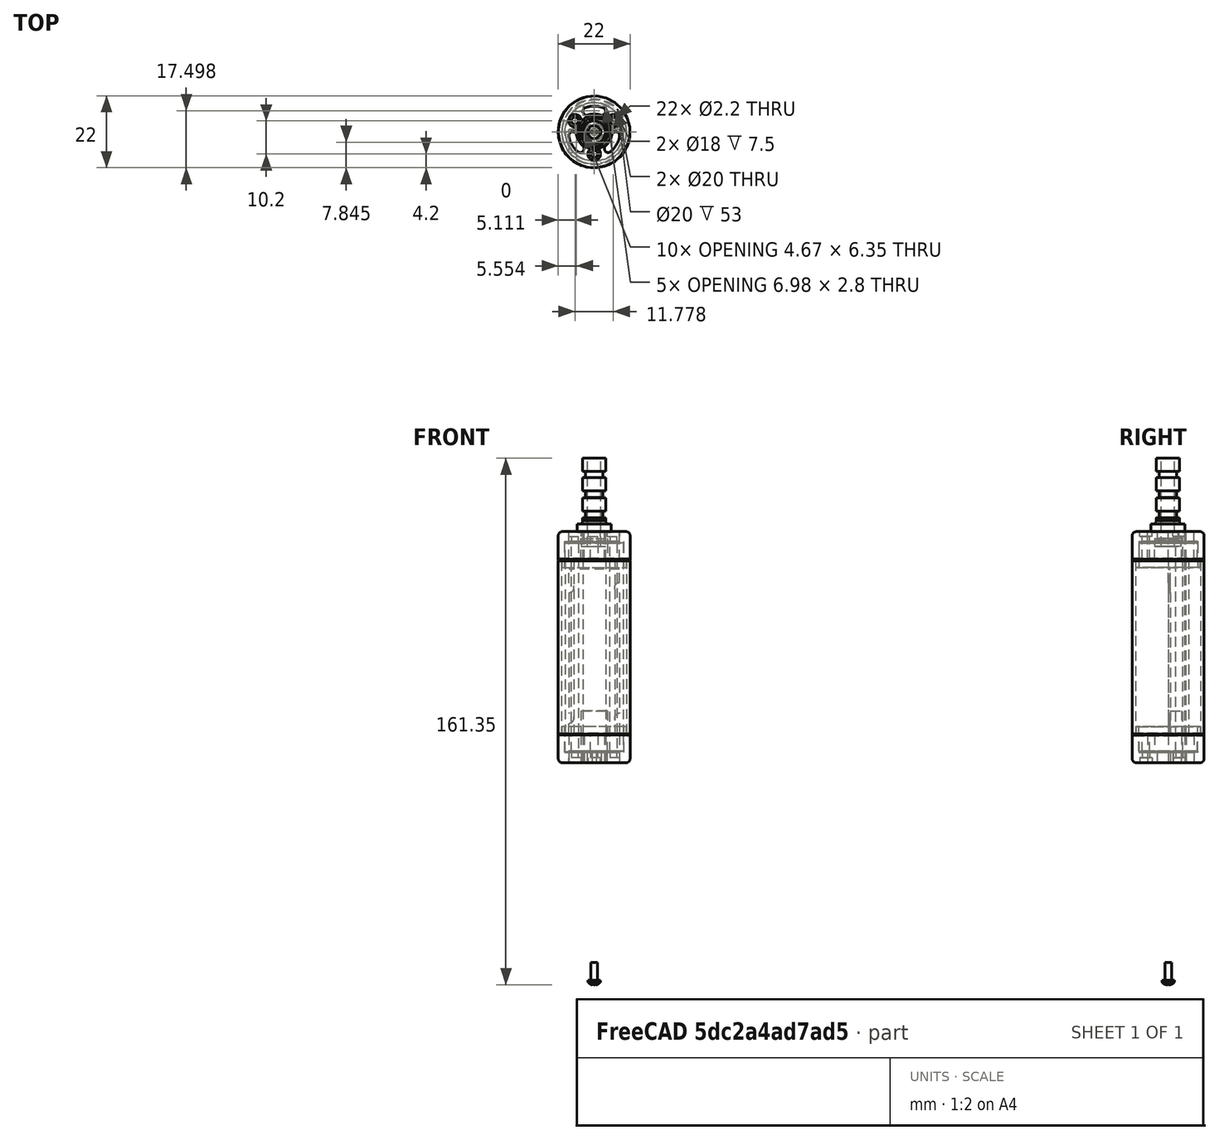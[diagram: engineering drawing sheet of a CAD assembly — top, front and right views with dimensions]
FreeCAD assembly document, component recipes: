
FREECAD ASSEMBLY — COMPONENT RECIPES ("Enclosure")

This assembly document has 17 components, labeled P0..P16 below (a component is one placed body or linked part). 17 of them carry a construction recipe — the FreeCAD feature program that regenerates the part from scratch, quoted from this document or its linked companion documents; the rest are supplied as boundary geometry only. No exploded tour is included for this assembly.
COMPONENT P0 — recipe-attached ("EndCap_Bottom", modeled in this document).
Construction recipe (the document's own serialized feature program — sketch geometry with constraints, then the solid features built on it; lengths are millimeters unless a unit is written):

FEATURE [Sketcher::SketchObject] Sketch  label="22mmCircle"
  ArcFitTolerance = 1e-06
  AttachmentSupport = -> [XY_Plane]
  ExternalTypes = [0]
  FullyConstrained = true
  MakeInternals = false
  MapMode = 5
  _ExternalGeoVersion = 0
  sketch-geometry (1):
    g0: Circle CenterX=0 CenterY=0 CenterZ=0 NormalX=0 NormalY=0 NormalZ=1 AngleXU=0 Radius=11
  constraints (2):
    c: Diameter(g0) = 22
    c: Coincident(g0,g-1)
FEATURE [PartDesign::Pad] Pad
  Direction = (0,0,1)
  Length = 8.5
  Length2 = 10
  Profile = -> Sketch
  ReferenceAxis = -> Sketch [N_Axis]
  SideType = 0
  Suppressed = false
  Type = 0
  Type2 = 0
FEATURE [Sketcher::SketchObject] Sketch001
  ArcFitTolerance = 1e-06
  AttachmentSupport = -> [Pad]
  ExternalTypes = [0]
  FullyConstrained = true
  MakeInternals = false
  MapMode = 5
  Placement = pos=(0,0,8.5) rot=(0,0,1;0rad)
  _ExternalGeoVersion = 0
  sketch-geometry (1):
    g0: Circle CenterX=0 CenterY=0 CenterZ=0 NormalX=0 NormalY=0 NormalZ=1 AngleXU=0 Radius=9.85
  constraints (2):
    c: Diameter(g0) = 19.7
    c: Coincident(g0,g-1)
FEATURE [PartDesign::Pad] Pad001
  BaseFeature = -> Pad
  Direction = (0,0,1)
  Length = 2.5
  Length2 = 10
  Profile = -> Sketch001
  ReferenceAxis = -> Sketch001 [N_Axis]
  SideType = 0
  Suppressed = false
  Type = 0
  Type2 = 0
FEATURE [Sketcher::SketchObject] Sketch002
  ArcFitTolerance = 1e-06
  AttachmentSupport = -> [Pad001]
  ExternalTypes = [0]
  FullyConstrained = true
  MakeInternals = false
  MapMode = 5
  Placement = pos=(0,0,11) rot=(0,0,1;0rad)
  _ExternalGeoVersion = 0
  sketch-geometry (1):
    g0: Circle CenterX=0 CenterY=0 CenterZ=0 NormalX=0 NormalY=0 NormalZ=1 AngleXU=0 Radius=9
  constraints (2):
    c: Diameter(g0) = 18
    c: Coincident(g0,g-1)
FEATURE [PartDesign::Pocket] Pocket
  BaseFeature = -> Pad001
  Direction = (0,0,-1)
  Length = 7.5
  Length2 = 5
  Profile = -> Sketch002
  ReferenceAxis = -> Sketch002 [N_Axis]
  SideType = 0
  Suppressed = false
  Type = 0
  Type2 = 0
FEATURE [Sketcher::SketchObject] Sketch003  label="BoltHoles_outer"
  ArcFitTolerance = 1e-06
  AttachmentSupport = -> [Pocket]
  ExternalGeometry = -> [Pocket]
  ExternalTypes = [0]
  FullyConstrained = true
  MakeInternals = false
  MapMode = 5
  Placement = pos=(0,0,0) rot=(1,0,0;3.14159rad)
  _ExternalGeoVersion = 0
  sketch-geometry (5):
    g0: Circle CenterX=0 CenterY=6.8 CenterZ=0 NormalX=0 NormalY=0 NormalZ=1 AngleXU=0 Radius=1.95
    g1: Circle CenterX=-5.88897 CenterY=-3.4 CenterZ=0 NormalX=0 NormalY=0 NormalZ=1 AngleXU=0 Radius=1.95
    g2: Circle CenterX=5.88897 CenterY=-3.4 CenterZ=0 NormalX=0 NormalY=0 NormalZ=1 AngleXU=0 Radius=1.95
    g3: LineSegment [constr] StartX=0 StartY=0 StartZ=0 EndX=5.88897 EndY=-3.4 EndZ=0
    g4: LineSegment [constr] StartX=-5.88897 StartY=-3.4 StartZ=0 EndX=0 EndY=0 EndZ=0
  constraints (13):
    c: Diameter(g0) = 3.9
    c: PointOnObject(g0,g-2)
    c: Diameter(g1) = 3.9
    c: Diameter(g2) = 3.9
    c: Distance(g-1,g0) = 6.8
    c: Distance(g-1,g1) = 6.8
    c: Distance(g-1,g2) = 6.8
    c: Coincident(g3,g-1)
    c: Coincident(g3,g2)
    c: Angle(g3,g-2) = 2.0944
    c: Coincident(g4,g1)
    c: Coincident(g4,g3)
    c: Angle(g-2,g4) = 2.0944
FEATURE [PartDesign::Pocket] Pocket001
  BaseFeature = -> Pocket
  Direction = (0,0,1)
  Length = 1.5
  Length2 = 5
  Profile = -> Sketch003
  ReferenceAxis = -> Sketch003 [N_Axis]
  SideType = 0
  Suppressed = false
  Type = 0
  Type2 = 0
FEATURE [PartDesign::Fillet] Fillet
  Base = -> Pocket001 [Edge2]
  BaseFeature = -> Pocket001
  Radius = 1.2
  SupportTransform = false
  Suppressed = false
  UseAllEdges = false
FEATURE [Sketcher::SketchObject] Sketch005  label="BoltHoles_inner"
  ArcFitTolerance = 1e-06
  AttachmentSupport = -> [Fillet]
  ExternalGeometry = -> [Fillet]
  ExternalTypes = [0]
  FullyConstrained = true
  MakeInternals = false
  MapMode = 5
  Placement = pos=(0,0,1.5) rot=(1,0,0;3.14159rad)
  _ExternalGeoVersion = 0
  sketch-geometry (3):
    g0: Circle CenterX=-5.88897 CenterY=-3.4 CenterZ=0 NormalX=0 NormalY=0 NormalZ=1 AngleXU=0 Radius=1.1
    g1: Circle CenterX=0 CenterY=6.8 CenterZ=0 NormalX=0 NormalY=0 NormalZ=1 AngleXU=0 Radius=1.1
    g2: Circle CenterX=5.88897 CenterY=-3.4 CenterZ=0 NormalX=0 NormalY=0 NormalZ=1 AngleXU=0 Radius=1.1
  constraints (6):
    c: Diameter(g0) = 2.2
    c: Coincident(g0,g-4)
    c: Diameter(g1) = 2.2
    c: Coincident(g1,g-3)
    c: Diameter(g2) = 2.2
    c: Coincident(g2,g-5)
FEATURE [PartDesign::Pocket] Pocket002
  BaseFeature = -> Fillet
  Direction = (0,0,1)
  Length = 2
  Length2 = 5
  Profile = -> Sketch005
  ReferenceAxis = -> Sketch005 [N_Axis]
  SideType = 0
  Suppressed = false
  Type = 0
  Type2 = 0
FEATURE [Sketcher::SketchObject] Sketch007  label="VentHoles"
  ArcFitTolerance = 1e-06
  AttachmentSupport = -> [Pocket002]
  ExternalGeometry = -> [Pocket002]
  ExternalTypes = [0]
  FullyConstrained = true
  MakeInternals = false
  MapMode = 5
  Placement = pos=(0,0,0) rot=(1,0,0;3.14159rad)
  _ExternalGeoVersion = 0
  sketch-geometry (58):
    g0: Circle [constr] CenterX=0 CenterY=0 CenterZ=0 NormalX=0 NormalY=0 NormalZ=1 AngleXU=0 Radius=7.9
    g1: Circle [constr] CenterX=0 CenterY=0 CenterZ=0 NormalX=0 NormalY=0 NormalZ=1 AngleXU=0 Radius=5.5
    g2: Circle [constr] CenterX=0 CenterY=0 CenterZ=0 NormalX=0 NormalY=0 NormalZ=1 AngleXU=0 Radius=4
    g3: Circle [constr] CenterX=0 CenterY=0 CenterZ=0 NormalX=0 NormalY=0 NormalZ=1 AngleXU=0 Radius=1.6
    g4: LineSegment [constr] StartX=0 StartY=0 StartZ=0 EndX=-6.29932 EndY=7.50724 EndZ=0
    g5: LineSegment [constr] StartX=0 StartY=0 StartZ=0 EndX=-9.65112 EndY=1.70175 EndZ=0
    g6: GeomPoint X=-5.07802 Y=6.05175 Z=0
    g7: GeomPoint X=-3.53533 Y=4.21324 Z=0
    g8: ArcOfCircle CenterX=-4.30668 CenterY=5.1325 CenterZ=0 NormalX=0 NormalY=0 NormalZ=1 AngleXU=0 Radius=1.2 StartAngle=5.41052 EndAngle=8.55211
    g9: GeomPoint X=-7.77998 Y=1.37182 Z=0
    g10: GeomPoint X=-5.41644 Y=0.955065 Z=0
    g11: ArcOfCircle CenterX=-6.59821 CenterY=1.16344 CenterZ=0 NormalX=0 NormalY=0 NormalZ=1 AngleXU=0 Radius=1.2 StartAngle=2.96706 EndAngle=6.10865
    g12: ArcOfCircle CenterX=0 CenterY=0 CenterZ=0 NormalX=0 NormalY=0 NormalZ=1 AngleXU=0 Radius=7.9 StartAngle=2.26893 EndAngle=2.96706
    g13: ArcOfCircle CenterX=-3e-16 CenterY=1e-16 CenterZ=0 NormalX=0 NormalY=0 NormalZ=1 AngleXU=0 Radius=5.5 StartAngle=2.26893 EndAngle=2.96706
    g14: LineSegment [constr] StartX=0 StartY=0 StartZ=0 EndX=6.29932 EndY=7.50724 EndZ=0
    g15: LineSegment [constr] StartX=-3e-16 StartY=1e-16 StartZ=0 EndX=9.65112 EndY=1.70175 EndZ=0
    g16: LineSegment [constr] StartX=0 StartY=0 StartZ=0 EndX=3.3518 EndY=-9.20899 EndZ=0
    g17: LineSegment [constr] StartX=0 StartY=0 StartZ=0 EndX=-3.3518 EndY=-9.20899 EndZ=0
    g18: GeomPoint X=5.07802 Y=6.05175 Z=0
    g19: GeomPoint X=3.53533 Y=4.21324 Z=0
    g20: GeomPoint X=5.41644 Y=0.955065 Z=0
    g21: GeomPoint X=7.77998 Y=1.37182 Z=0
    g22: GeomPoint X=-1.88111 Y=-5.16831 Z=0
    g23: GeomPoint X=-2.70196 Y=-7.42357 Z=0
    g24: GeomPoint X=1.88111 Y=-5.16831 Z=0
    g25: GeomPoint X=2.70196 Y=-7.42357 Z=0
    g26: ArcOfCircle CenterX=4.30668 CenterY=5.1325 CenterZ=0 NormalX=0 NormalY=0 NormalZ=1 AngleXU=0 Radius=1.2 StartAngle=0.872665 EndAngle=4.01426
    g27: ArcOfCircle CenterX=6.59821 CenterY=1.16344 CenterZ=0 NormalX=0 NormalY=0 NormalZ=1 AngleXU=0 Radius=1.2 StartAngle=3.31613 EndAngle=6.45772
    g28: ArcOfCircle CenterX=-3e-16 CenterY=0 CenterZ=0 NormalX=0 NormalY=0 NormalZ=1 AngleXU=0 Radius=7.9 StartAngle=0.174533 EndAngle=0.872665
    g29: ArcOfCircle CenterX=-1e-16 CenterY=9e-16 CenterZ=0 NormalX=0 NormalY=0 NormalZ=1 AngleXU=0 Radius=5.5 StartAngle=0.174533 EndAngle=0.872665
    g30: ArcOfCircle CenterX=-2.29153 CenterY=-6.29594 CenterZ=0 NormalX=0 NormalY=0 NormalZ=1 AngleXU=0 Radius=1.2 StartAngle=1.22173 EndAngle=4.36332
    g31: ArcOfCircle CenterX=2.29153 CenterY=-6.29594 CenterZ=0 NormalX=0 NormalY=0 NormalZ=1 AngleXU=0 Radius=1.2 StartAngle=5.06145 EndAngle=8.20305
    g32: ArcOfCircle CenterX=-1.5e-15 CenterY=2e-16 CenterZ=0 NormalX=0 NormalY=0 NormalZ=1 AngleXU=0 Radius=7.9 StartAngle=4.36332 EndAngle=5.06145
    g33: ArcOfCircle CenterX=-2e-16 CenterY=-2e-16 CenterZ=0 NormalX=0 NormalY=0 NormalZ=1 AngleXU=0 Radius=5.5 StartAngle=4.36332 EndAngle=5.06145
    g34: GeomPoint X=-2.57115 Y=3.06418 Z=0
    g35: GeomPoint X=-1.02846 Y=1.22567 Z=0
    g36: GeomPoint X=-3.93923 Y=0.694593 Z=0
    g37: GeomPoint X=-1.57569 Y=0.277837 Z=0
    g38: ArcOfCircle CenterX=-1.79981 CenterY=2.14492 CenterZ=0 NormalX=0 NormalY=0 NormalZ=1 AngleXU=0 Radius=1.2 StartAngle=5.41052 EndAngle=8.55211
    g39: ArcOfCircle CenterX=-2.75746 CenterY=0.486215 CenterZ=0 NormalX=0 NormalY=0 NormalZ=1 AngleXU=0 Radius=1.2 StartAngle=2.96706 EndAngle=6.10865
    g40: ArcOfCircle CenterX=-6e-16 CenterY=-4e-16 CenterZ=0 NormalX=0 NormalY=0 NormalZ=1 AngleXU=0 Radius=4 StartAngle=2.26893 EndAngle=2.96706
    g41: ArcOfCircle CenterX=1e-16 CenterY=1e-16 CenterZ=0 NormalX=0 NormalY=0 NormalZ=1 AngleXU=0 Radius=1.6 StartAngle=2.26893 EndAngle=2.96706
    g42: GeomPoint X=1.02846 Y=1.22567 Z=0
    g43: GeomPoint X=2.57115 Y=3.06418 Z=0
    g44: GeomPoint X=1.57569 Y=0.277837 Z=0
    g45: GeomPoint X=3.93923 Y=0.694593 Z=0
    g46: GeomPoint X=1.36808 Y=-3.75877 Z=0
    g47: GeomPoint X=0.547232 Y=-1.50351 Z=0
    g48: GeomPoint X=-1.36808 Y=-3.75877 Z=0
    g49: GeomPoint X=-0.547232 Y=-1.50351 Z=0
    g50: ArcOfCircle CenterX=0 CenterY=0 CenterZ=0 NormalX=0 NormalY=0 NormalZ=1 AngleXU=0 Radius=1.6 StartAngle=4.36332 EndAngle=5.06145
    g51: ArcOfCircle CenterX=-3e-16 CenterY=-4e-16 CenterZ=0 NormalX=0 NormalY=0 NormalZ=1 AngleXU=0 Radius=4 StartAngle=4.36332 EndAngle=5.06145
    g52: ArcOfCircle CenterX=0.957656 CenterY=-2.63114 CenterZ=0 NormalX=0 NormalY=0 NormalZ=1 AngleXU=0 Radius=1.2 StartAngle=5.06145 EndAngle=8.20305
    g53: ArcOfCircle CenterX=-0.957656 CenterY=-2.63114 CenterZ=0 NormalX=0 NormalY=0 NormalZ=1 AngleXU=0 Radius=1.2 StartAngle=1.22173 EndAngle=4.36332
    g54: ArcOfCircle CenterX=1.79981 CenterY=2.14492 CenterZ=0 NormalX=0 NormalY=0 NormalZ=1 AngleXU=0 Radius=1.2 StartAngle=0.872665 EndAngle=4.01426
    g55: ArcOfCircle CenterX=2.75746 CenterY=0.486215 CenterZ=0 NormalX=0 NormalY=0 NormalZ=1 AngleXU=0 Radius=1.2 StartAngle=3.31613 EndAngle=6.45772
    g56: ArcOfCircle CenterX=1e-16 CenterY=1e-16 CenterZ=0 NormalX=0 NormalY=0 NormalZ=1 AngleXU=0 Radius=1.6 StartAngle=0.174533 EndAngle=0.872665
    g57: ArcOfCircle CenterX=-1.6749e-12 CenterY=-9.675e-13 CenterZ=0 NormalX=0 NormalY=0 NormalZ=1 AngleXU=0 Radius=4 StartAngle=0.174533 EndAngle=0.872665
  constraints (146):
    c: Diameter(g0) = 15.8
    c: Coincident(g0,g-1)
    c: Diameter(g1) = 11
    c: Coincident(g1,g0)
    c: Diameter(g2) = 8
    c: Coincident(g2,g0)
    c: Diameter(g3) = 3.2
    c: Coincident(g3,g0)
    c: Coincident(g4,g0)
    c: PointOnObject(g4,g-3)
    c: Angle(g-2,g4) = 0.698132
    c: Coincident(g5,g0)
    c: PointOnObject(g5,g-3)
    c: Angle(g4,g5) = 0.698132
    c: PointOnObject(g6,g0)
    c: PointOnObject(g6,g4)
    c: PointOnObject(g7,g1)
    c: PointOnObject(g7,g4)
    c: Coincident(g8,g6)
    c: Coincident(g8,g7)
    c: PointOnObject(g8,g4)
    c: PointOnObject(g9,g0)
    c: PointOnObject(g10,g1)
    c: PointOnObject(g10,g5)
    c: PointOnObject(g9,g5)
    c: Coincident(g11,g9)
    c: Coincident(g11,g10)
    c: PointOnObject(g11,g5)
    c: Equal(g0,g12)
    c: Coincident(g12,g6)
    c: Coincident(g12,g9)
    c: Equal(g13,g1)
    c: Coincident(g13,g7)
    c: Coincident(g13,g10)
    c: Coincident(g14,g12)
    c: PointOnObject(g14,g-3)
    c: Coincident(g15,g13)
    c: PointOnObject(g15,g-3)
    c: Angle(g14,g-2) = 0.698132
    c: Angle(g15,g14) = 0.698132
    c: Coincident(g16,g0)
    c: PointOnObject(g16,g-3)
    c: Coincident(g17,g0)
    c: PointOnObject(g17,g-3)
    c: Angle(g-2,g16) = 0.349066
    c: Angle(g17,g16) = 0.698132
    c: PointOnObject(g18,g14)
    c: PointOnObject(g19,g14)
    c: PointOnObject(g20,g15)
    c: PointOnObject(g21,g15)
    c: PointOnObject(g18,g0)
    c: PointOnObject(g19,g1)
    c: PointOnObject(g20,g1)
    c: PointOnObject(g21,g0)
    c: PointOnObject(g22,g17)
    c: PointOnObject(g23,g17)
    c: PointOnObject(g24,g16)
    c: PointOnObject(g25,g16)
    c: PointOnObject(g25,g0)
    c: PointOnObject(g24,g1)
    c: PointOnObject(g22,g1)
    c: PointOnObject(g23,g0)
    c: Coincident(g26,g18)
    c: Coincident(g26,g19)
    c: Coincident(g27,g20)
    c: Coincident(g27,g21)
    c: PointOnObject(g27,g15)
    c: PointOnObject(g26,g14)
    c: Coincident(g28,g18)
    c: Coincident(g28,g21)
    c: Equal(g0,g28)
    c: Coincident(g29,g19)
    c: Coincident(g29,g20)
    c: Equal(g29,g1)
    c: Coincident(g30,g22)
    c: Coincident(g30,g23)
    c: Coincident(g31,g25)
    c: Coincident(g31,g24)
    c: PointOnObject(g31,g16)
    c: PointOnObject(g30,g17)
    c: Coincident(g33,g24)
    c: Coincident(g33,g22)
    c: Coincident(g32,g23)
    c: Coincident(g32,g25)
    c: Equal(g33,g1)
    c: Equal(g32,g0)
    c: PointOnObject(g34,g4)
    c: PointOnObject(g35,g4)
    c: PointOnObject(g36,g5)
    c: PointOnObject(g37,g5)
    c: PointOnObject(g34,g2)
    c: PointOnObject(g35,g3)
    c: PointOnObject(g37,g3)
    c: PointOnObject(g36,g2)
    c: Coincident(g38,g35)
    c: Coincident(g38,g34)
    c: Coincident(g39,g37)
    c: Coincident(g39,g36)
    c: PointOnObject(g39,g5)
    c: PointOnObject(g38,g4)
    c: Coincident(g41,g35)
    c: Coincident(g41,g37)
    c: Coincident(g40,g34)
    c: Coincident(g40,g36)
    c: Equal(g40,g2)
    c: Equal(g41,g3)
    c: PointOnObject(g42,g14)
    c: PointOnObject(g43,g14)
    c: PointOnObject(g44,g15)
    c: PointOnObject(g45,g15)
    c: PointOnObject(g46,g16)
    c: PointOnObject(g47,g16)
    c: PointOnObject(g48,g17)
    c: PointOnObject(g49,g17)
    c: PointOnObject(g47,g3)
    c: PointOnObject(g46,g2)
    c: PointOnObject(g48,g2)
    c: PointOnObject(g49,g3)
    c: PointOnObject(g45,g2)
    c: PointOnObject(g43,g2)
    c: PointOnObject(g42,g3)
    c: PointOnObject(g44,g3)
    c: Coincident(g51,g46)
    c: Coincident(g51,g48)
    c: Coincident(g50,g49)
    c: Coincident(g47,g50)
    c: Equal(g51,g2)
    c: Equal(g50,g3)
    c: Coincident(g52,g47)
    c: Coincident(g52,g46)
    c: Coincident(g53,g48)
    c: Coincident(g53,g49)
    c: PointOnObject(g53,g17)
    c: PointOnObject(g52,g16)
    c: Coincident(g54,g42)
    c: Coincident(g54,g43)
    c: Coincident(g55,g44)
    c: Coincident(g55,g45)
    c: PointOnObject(g55,g15)
    c: PointOnObject(g54,g14)
    c: Coincident(g42,g56)
    c: Coincident(g56,g44)
    c: Coincident(g57,g43)
    c: Coincident(g57,g45)
    c: Equal(g56,g3)
    c: Equal(g57,g2)
FEATURE [PartDesign::Pocket] Pocket003
  BaseFeature = -> Pocket002
  Direction = (0,0,1)
  Length = 3.5
  Length2 = 5
  Profile = -> Sketch007
  ReferenceAxis = -> Sketch007 [N_Axis]
  SideType = 0
  Suppressed = false
  Type = 0
  Type2 = 0
FEATURE [PartDesign::Body] Body  label="EndCap_Bottom"
  AllowCompound = false
  Group = -> [Sketch,Pad,Sketch001,Pad001,Sketch002,Pocket,Sketch003,Pocket001,Fillet,Sketch005,Pocket002,Sketch007,Pocket003]
  Origin = -> Origin
  Placement = pos=(0,1e-05,68.2) rot=(0,0,1;0rad)
  Tip = -> Pocket003
COMPONENT P1 — recipe-attached ("QuartzTube", modeled in this document).
Construction recipe (the document's own serialized feature program — sketch geometry with constraints, then the solid features built on it; lengths are millimeters unless a unit is written):

FEATURE [Sketcher::SketchObject] Sketch006
  ArcFitTolerance = 1e-06
  AttachmentSupport = -> [XY_Plane001]
  ExternalTypes = [0]
  FullyConstrained = true
  MakeInternals = false
  MapMode = 5
  _ExternalGeoVersion = 0
  sketch-geometry (2):
    g0: Circle CenterX=0 CenterY=0 CenterZ=0 NormalX=0 NormalY=0 NormalZ=1 AngleXU=0 Radius=11
    g1: Circle CenterX=0 CenterY=0 CenterZ=0 NormalX=0 NormalY=0 NormalZ=1 AngleXU=0 Radius=10
  constraints (4):
    c: Diameter(g0) = 22
    c: Coincident(g0,g-1)
    c: Diameter(g1) = 20
    c: Coincident(g1,g0)
FEATURE [PartDesign::Pad] Pad002
  Direction = (0,0,1)
  Length = 53
  Length2 = 10
  Profile = -> Sketch006
  ReferenceAxis = -> Sketch006 [N_Axis]
  SideType = 0
  Suppressed = false
  Type = 0
  Type2 = 0
FEATURE [PartDesign::Body] Body001  label="QuartzTube"
  AllowCompound = false
  Group = -> [Sketch006,Pad002]
  Origin = -> Origin001
  Placement = pos=(0,0,77) rot=(0,0,1;0rad)
  Tip = -> Pad002
COMPONENT P2 — recipe-attached ("EndCap_Top", modeled in this document).
Construction recipe (the document's own serialized feature program — sketch geometry with constraints, then the solid features built on it; lengths are millimeters unless a unit is written):

FEATURE [Sketcher::SketchObject] Sketch008  label="22mmCircle001"
  ArcFitTolerance = 1e-06
  AttachmentSupport = -> [XY_Plane002]
  ExternalTypes = [0]
  FullyConstrained = true
  MakeInternals = false
  MapMode = 5
  _ExternalGeoVersion = 0
  sketch-geometry (1):
    g0: Circle CenterX=0 CenterY=0 CenterZ=0 NormalX=0 NormalY=0 NormalZ=1 AngleXU=0 Radius=11
  constraints (2):
    c: Diameter(g0) = 22
    c: Coincident(g0,g-1)
FEATURE [PartDesign::Pad] Pad003
  Direction = (0,0,1)
  Length = 8.5
  Length2 = 10
  Profile = -> Sketch008
  ReferenceAxis = -> Sketch008 [N_Axis]
  SideType = 0
  Suppressed = false
  Type = 0
  Type2 = 0
FEATURE [Sketcher::SketchObject] Sketch009
  ArcFitTolerance = 1e-06
  AttachmentSupport = -> [Pad003]
  ExternalTypes = [0]
  FullyConstrained = true
  MakeInternals = false
  MapMode = 5
  Placement = pos=(0,0,8.5) rot=(0,0,1;0rad)
  _ExternalGeoVersion = 0
  sketch-geometry (1):
    g0: Circle CenterX=0 CenterY=0 CenterZ=0 NormalX=0 NormalY=0 NormalZ=1 AngleXU=0 Radius=9.85
  constraints (2):
    c: Diameter(g0) = 19.7
    c: Coincident(g0,g-1)
FEATURE [PartDesign::Pad] Pad004
  BaseFeature = -> Pad003
  Direction = (0,0,1)
  Length = 2.5
  Length2 = 10
  Profile = -> Sketch009
  ReferenceAxis = -> Sketch009 [N_Axis]
  SideType = 0
  Suppressed = false
  Type = 0
  Type2 = 0
FEATURE [Sketcher::SketchObject] Sketch010
  ArcFitTolerance = 1e-06
  AttachmentSupport = -> [Pad004]
  ExternalTypes = [0]
  FullyConstrained = true
  MakeInternals = false
  MapMode = 5
  Placement = pos=(0,0,11) rot=(0,0,1;0rad)
  _ExternalGeoVersion = 0
  sketch-geometry (1):
    g0: Circle CenterX=0 CenterY=0 CenterZ=0 NormalX=0 NormalY=0 NormalZ=1 AngleXU=0 Radius=9
  constraints (2):
    c: Diameter(g0) = 18
    c: Coincident(g0,g-1)
FEATURE [PartDesign::Pocket] Pocket004
  BaseFeature = -> Pad004
  Direction = (0,0,-1)
  Length = 7.5
  Length2 = 5
  Profile = -> Sketch010
  ReferenceAxis = -> Sketch010 [N_Axis]
  SideType = 0
  Suppressed = false
  Type = 0
  Type2 = 0
FEATURE [Sketcher::SketchObject] Sketch011  label="BoltHoles_outer001"
  ArcFitTolerance = 1e-06
  AttachmentSupport = -> [Pocket004]
  ExternalGeometry = -> [Pocket004]
  ExternalTypes = [0]
  FullyConstrained = true
  MakeInternals = false
  MapMode = 5
  Placement = pos=(0,0,0) rot=(1,0,0;3.14159rad)
  _ExternalGeoVersion = 0
  sketch-geometry (5):
    g0: Circle CenterX=0 CenterY=6.8 CenterZ=0 NormalX=0 NormalY=0 NormalZ=1 AngleXU=0 Radius=1.95
    g1: Circle CenterX=-5.88897 CenterY=-3.4 CenterZ=0 NormalX=0 NormalY=0 NormalZ=1 AngleXU=0 Radius=1.95
    g2: Circle CenterX=5.88897 CenterY=-3.4 CenterZ=0 NormalX=0 NormalY=0 NormalZ=1 AngleXU=0 Radius=1.95
    g3: LineSegment [constr] StartX=0 StartY=0 StartZ=0 EndX=5.88897 EndY=-3.4 EndZ=0
    g4: LineSegment [constr] StartX=-5.88897 StartY=-3.4 StartZ=0 EndX=0 EndY=0 EndZ=0
  constraints (13):
    c: Diameter(g0) = 3.9
    c: PointOnObject(g0,g-2)
    c: Diameter(g1) = 3.9
    c: Diameter(g2) = 3.9
    c: Distance(g-1,g0) = 6.8
    c: Distance(g-1,g1) = 6.8
    c: Distance(g-1,g2) = 6.8
    c: Coincident(g3,g-1)
    c: Coincident(g3,g2)
    c: Angle(g3,g-2) = 2.0944
    c: Coincident(g4,g1)
    c: Coincident(g4,g3)
    c: Angle(g-2,g4) = 2.0944
FEATURE [PartDesign::Pocket] Pocket005
  BaseFeature = -> Pocket004
  Direction = (0,0,1)
  Length = 1.5
  Length2 = 5
  Profile = -> Sketch011
  ReferenceAxis = -> Sketch011 [N_Axis]
  SideType = 0
  Suppressed = false
  Type = 0
  Type2 = 0
FEATURE [PartDesign::Fillet] Fillet001
  Base = -> Pocket005 [Edge2]
  BaseFeature = -> Pocket005
  Radius = 1.2
  SupportTransform = false
  Suppressed = false
  UseAllEdges = false
FEATURE [Sketcher::SketchObject] Sketch012  label="BoltHoles_inner001"
  ArcFitTolerance = 1e-06
  AttachmentSupport = -> [Fillet001]
  ExternalGeometry = -> [Fillet001]
  ExternalTypes = [0]
  FullyConstrained = true
  MakeInternals = false
  MapMode = 5
  Placement = pos=(0,0,1.5) rot=(1,0,0;3.14159rad)
  _ExternalGeoVersion = 0
  sketch-geometry (3):
    g0: Circle CenterX=-5.88897 CenterY=-3.4 CenterZ=0 NormalX=0 NormalY=0 NormalZ=1 AngleXU=0 Radius=1.1
    g1: Circle CenterX=0 CenterY=6.8 CenterZ=0 NormalX=0 NormalY=0 NormalZ=1 AngleXU=0 Radius=1.1
    g2: Circle CenterX=5.88897 CenterY=-3.4 CenterZ=0 NormalX=0 NormalY=0 NormalZ=1 AngleXU=0 Radius=1.1
  constraints (6):
    c: Diameter(g0) = 2.2
    c: Coincident(g0,g-4)
    c: Diameter(g1) = 2.2
    c: Coincident(g1,g-3)
    c: Diameter(g2) = 2.2
    c: Coincident(g2,g-5)
FEATURE [PartDesign::Pocket] Pocket006
  BaseFeature = -> Fillet001
  Direction = (0,0,1)
  Length = 2
  Length2 = 5
  Profile = -> Sketch012
  ReferenceAxis = -> Sketch012 [N_Axis]
  SideType = 0
  Suppressed = false
  Type = 0
  Type2 = 0
FEATURE [Sketcher::SketchObject] Sketch013  label="VentHoles001"
  ArcFitTolerance = 1e-06
  AttachmentSupport = -> [Pocket006]
  ExternalGeometry = -> [Pocket006]
  ExternalTypes = [0]
  FullyConstrained = true
  MakeInternals = false
  MapMode = 5
  Placement = pos=(0,0,0) rot=(1,0,0;3.14159rad)
  _ExternalGeoVersion = 0
  sketch-geometry (33):
    g0: Circle [constr] CenterX=0 CenterY=0 CenterZ=0 NormalX=0 NormalY=0 NormalZ=1 AngleXU=0 Radius=7.9
    g1: Circle [constr] CenterX=0 CenterY=0 CenterZ=0 NormalX=0 NormalY=0 NormalZ=1 AngleXU=0 Radius=5.5
    g2: Circle CenterX=0 CenterY=0 CenterZ=0 NormalX=0 NormalY=0 NormalZ=1 AngleXU=0 Radius=3.3
    g3: LineSegment [constr] StartX=0 StartY=0 StartZ=0 EndX=-6.29932 EndY=7.50724 EndZ=0
    g4: LineSegment [constr] StartX=0 StartY=0 StartZ=0 EndX=-9.65112 EndY=1.70175 EndZ=0
    g5: GeomPoint X=-5.07802 Y=6.05175 Z=0
    g6: GeomPoint X=-3.53533 Y=4.21324 Z=0
    g7: ArcOfCircle CenterX=-4.30668 CenterY=5.1325 CenterZ=0 NormalX=0 NormalY=0 NormalZ=1 AngleXU=0 Radius=1.2 StartAngle=5.41052 EndAngle=8.55211
    g8: GeomPoint X=-7.77998 Y=1.37182 Z=0
    g9: GeomPoint X=-5.41644 Y=0.955065 Z=0
    g10: ArcOfCircle CenterX=-6.59821 CenterY=1.16344 CenterZ=0 NormalX=0 NormalY=0 NormalZ=1 AngleXU=0 Radius=1.2 StartAngle=2.96706 EndAngle=6.10865
    g11: ArcOfCircle CenterX=4e-16 CenterY=-2e-16 CenterZ=0 NormalX=0 NormalY=0 NormalZ=1 AngleXU=0 Radius=7.9 StartAngle=2.26893 EndAngle=2.96706
    g12: ArcOfCircle CenterX=-3e-16 CenterY=-2e-16 CenterZ=0 NormalX=0 NormalY=0 NormalZ=1 AngleXU=0 Radius=5.5 StartAngle=2.26893 EndAngle=2.96706
    g13: LineSegment [constr] StartX=4e-16 StartY=-2e-16 StartZ=0 EndX=6.29932 EndY=7.50724 EndZ=0
    g14: LineSegment [constr] StartX=-3e-16 StartY=-2e-16 StartZ=0 EndX=9.65112 EndY=1.70175 EndZ=0
    g15: LineSegment [constr] StartX=0 StartY=0 StartZ=0 EndX=3.3518 EndY=-9.20899 EndZ=0
    g16: LineSegment [constr] StartX=0 StartY=0 StartZ=0 EndX=-3.3518 EndY=-9.20899 EndZ=0
    g17: GeomPoint X=5.07802 Y=6.05175 Z=0
    g18: GeomPoint X=3.53533 Y=4.21324 Z=0
    g19: GeomPoint X=5.41644 Y=0.955065 Z=0
    g20: GeomPoint X=7.77998 Y=1.37182 Z=0
    g21: GeomPoint X=-1.88111 Y=-5.16831 Z=0
    g22: GeomPoint X=-2.70196 Y=-7.42357 Z=0
    g23: GeomPoint X=1.88111 Y=-5.16831 Z=0
    g24: GeomPoint X=2.70196 Y=-7.42357 Z=0
    g25: ArcOfCircle CenterX=4.30668 CenterY=5.1325 CenterZ=0 NormalX=0 NormalY=0 NormalZ=1 AngleXU=0 Radius=1.2 StartAngle=0.872665 EndAngle=4.01426
    g26: ArcOfCircle CenterX=6.59821 CenterY=1.16344 CenterZ=0 NormalX=0 NormalY=0 NormalZ=1 AngleXU=0 Radius=1.2 StartAngle=3.31613 EndAngle=6.45772
    g27: ArcOfCircle CenterX=0 CenterY=0 CenterZ=0 NormalX=0 NormalY=0 NormalZ=1 AngleXU=0 Radius=7.9 StartAngle=0.174533 EndAngle=0.872665
    g28: ArcOfCircle CenterX=2e-16 CenterY=3e-16 CenterZ=0 NormalX=0 NormalY=0 NormalZ=1 AngleXU=0 Radius=5.5 StartAngle=0.174533 EndAngle=0.872665
    g29: ArcOfCircle CenterX=-2.29153 CenterY=-6.29594 CenterZ=0 NormalX=0 NormalY=0 NormalZ=1 AngleXU=0 Radius=1.2 StartAngle=1.22173 EndAngle=4.36332
    g30: ArcOfCircle CenterX=2.29153 CenterY=-6.29594 CenterZ=0 NormalX=0 NormalY=0 NormalZ=1 AngleXU=0 Radius=1.2 StartAngle=5.06145 EndAngle=8.20305
    g31: ArcOfCircle CenterX=-8e-16 CenterY=1.1e-15 CenterZ=0 NormalX=0 NormalY=0 NormalZ=1 AngleXU=0 Radius=7.9 StartAngle=4.36332 EndAngle=5.06145
    g32: ArcOfCircle CenterX=-2.6e-15 CenterY=1e-16 CenterZ=0 NormalX=0 NormalY=0 NormalZ=1 AngleXU=0 Radius=5.5 StartAngle=4.36332 EndAngle=5.06145
  constraints (84):
    c: Diameter(g0) = 15.8
    c: Coincident(g0,g-1)
    c: Diameter(g1) = 11
    c: Coincident(g1,g0)
    c: Diameter(g2) = 6.6
    c: Coincident(g2,g0)
    c: Coincident(g3,g0)
    c: PointOnObject(g3,g-3)
    c: Angle(g-2,g3) = 0.698132
    c: Coincident(g4,g0)
    c: PointOnObject(g4,g-3)
    c: Angle(g3,g4) = 0.698132
    c: PointOnObject(g5,g0)
    c: PointOnObject(g5,g3)
    c: PointOnObject(g6,g1)
    c: PointOnObject(g6,g3)
    c: Coincident(g7,g5)
    c: Coincident(g7,g6)
    c: PointOnObject(g7,g3)
    c: PointOnObject(g8,g0)
    c: PointOnObject(g9,g1)
    c: PointOnObject(g9,g4)
    c: PointOnObject(g8,g4)
    c: Coincident(g10,g8)
    c: Coincident(g10,g9)
    c: PointOnObject(g10,g4)
    c: Equal(g0,g11)
    c: Coincident(g11,g5)
    c: Coincident(g11,g8)
    c: Equal(g12,g1)
    c: Coincident(g12,g6)
    c: Coincident(g12,g9)
    c: Coincident(g13,g11)
    c: PointOnObject(g13,g-3)
    c: Coincident(g14,g12)
    c: PointOnObject(g14,g-3)
    c: Angle(g13,g-2) = 0.698132
    c: Angle(g14,g13) = 0.698132
    c: Coincident(g15,g0)
    c: PointOnObject(g15,g-3)
    c: Coincident(g16,g0)
    c: PointOnObject(g16,g-3)
    c: Angle(g-2,g15) = 0.349066
    c: Angle(g16,g15) = 0.698132
    c: PointOnObject(g17,g13)
    c: PointOnObject(g18,g13)
    c: PointOnObject(g19,g14)
    c: PointOnObject(g20,g14)
    c: PointOnObject(g17,g0)
    c: PointOnObject(g18,g1)
    c: PointOnObject(g19,g1)
    c: PointOnObject(g20,g0)
    c: PointOnObject(g21,g16)
    c: PointOnObject(g22,g16)
    c: PointOnObject(g23,g15)
    c: PointOnObject(g24,g15)
    c: PointOnObject(g24,g0)
    c: PointOnObject(g23,g1)
    c: PointOnObject(g21,g1)
    c: PointOnObject(g22,g0)
    c: Coincident(g25,g17)
    c: Coincident(g25,g18)
    c: Coincident(g26,g19)
    c: Coincident(g26,g20)
    c: PointOnObject(g26,g14)
    c: PointOnObject(g25,g13)
    c: Coincident(g27,g17)
    c: Coincident(g27,g20)
    c: Equal(g0,g27)
    c: Coincident(g28,g18)
    c: Coincident(g28,g19)
    c: Equal(g28,g1)
    c: Coincident(g29,g21)
    c: Coincident(g29,g22)
    c: Coincident(g30,g24)
    c: Coincident(g30,g23)
    c: PointOnObject(g30,g15)
    c: PointOnObject(g29,g16)
    c: Coincident(g32,g23)
    c: Coincident(g32,g21)
    c: Coincident(g31,g22)
    c: Coincident(g31,g24)
    c: Equal(g32,g1)
    c: Equal(g31,g0)
FEATURE [PartDesign::Pocket] Pocket007
  BaseFeature = -> Pocket006
  Direction = (0,0,1)
  Length = 3.5
  Length2 = 5
  Profile = -> Sketch013
  ReferenceAxis = -> Sketch013 [N_Axis]
  SideType = 0
  Suppressed = false
  Type = 0
  Type2 = 0
FEATURE [Sketcher::SketchObject] Sketch014
  ArcFitTolerance = 1e-06
  AttachmentSupport = -> [Pocket007]
  ExternalTypes = [0]
  FullyConstrained = true
  MakeInternals = false
  MapMode = 5
  Placement = pos=(0,0,3.5) rot=(0,0,1;0rad)
  _ExternalGeoVersion = 0
  sketch-geometry (1):
    g0: Circle CenterX=0 CenterY=0 CenterZ=0 NormalX=0 NormalY=0 NormalZ=1 AngleXU=0 Radius=4.1
  constraints (2):
    c: Diameter(g0) = 8.2
    c: Coincident(g0,g-1)
FEATURE [PartDesign::Pocket] Pocket008
  BaseFeature = -> Pocket007
  Direction = (0,0,-1)
  Length = 1.4
  Length2 = 5
  Profile = -> Sketch014
  ReferenceAxis = -> Sketch014 [N_Axis]
  SideType = 0
  Suppressed = false
  Type = 0
  Type2 = 0
FEATURE [PartDesign::Body] Body002  label="EndCap_Top"
  AllowCompound = false
  Group = -> [Sketch008,Pad003,Sketch009,Pad004,Sketch010,Pocket004,Sketch011,Pocket005,Fillet001,Sketch012,Pocket006,Sketch013,Pocket007,Sketch014,Pocket008]
  Origin = -> Origin002
  Placement = pos=(2.39184e-06,1e-05,139) rot=(0,1.00436,0;3.14159rad)
  Tip = -> Pocket008
COMPONENT P3 — recipe-attached ("RubberRing_Top", modeled in this document).
Construction recipe (the document's own serialized feature program — sketch geometry with constraints, then the solid features built on it; lengths are millimeters unless a unit is written):

FEATURE [Sketcher::SketchObject] Sketch016
  ArcFitTolerance = 1e-06
  AttachmentSupport = -> [XY_Plane004]
  ExternalTypes = [0]
  FullyConstrained = true
  MakeInternals = false
  MapMode = 5
  _ExternalGeoVersion = 0
  sketch-geometry (2):
    g0: Circle CenterX=0 CenterY=0 CenterZ=0 NormalX=0 NormalY=0 NormalZ=1 AngleXU=0 Radius=11
    g1: Circle CenterX=0 CenterY=0 CenterZ=0 NormalX=0 NormalY=0 NormalZ=1 AngleXU=0 Radius=10
  constraints (4):
    c: Diameter(g0) = 22
    c: Coincident(g0,g-1)
    c: Diameter(g1) = 20
    c: Coincident(g1,g0)
FEATURE [PartDesign::Pad] Pad006
  Direction = (0,0,1)
  Length = 0.75
  Length2 = 10
  Profile = -> Sketch016
  ReferenceAxis = -> Sketch016 [N_Axis]
  SideType = 0
  Suppressed = false
  Type = 0
  Type2 = 0
FEATURE [PartDesign::Fillet] Fillet002
  Base = -> Pad006 [Edge3]
  BaseFeature = -> Pad006
  Radius = 0.35
  SupportTransform = false
  Suppressed = false
  UseAllEdges = false
FEATURE [PartDesign::Fillet] Fillet003
  Base = -> Fillet002 [Edge3]
  BaseFeature = -> Fillet002
  Radius = 0.35
  SupportTransform = false
  Suppressed = false
  UseAllEdges = false
FEATURE [PartDesign::Fillet] Fillet004
  Base = -> Fillet003 [Edge9]
  BaseFeature = -> Fillet003
  Radius = 0.35
  SupportTransform = false
  Suppressed = false
  UseAllEdges = false
FEATURE [PartDesign::Fillet] Fillet005
  Base = -> Fillet004 [Edge8]
  BaseFeature = -> Fillet004
  Radius = 0.35
  SupportTransform = false
  Suppressed = false
  UseAllEdges = false
FEATURE [PartDesign::Body] Body004  label="RubberRing_Top"
  AllowCompound = false
  Group = -> [Sketch016,Pad006,Fillet002,Fillet003,Fillet004,Fillet005]
  Origin = -> Origin004
  Placement = pos=(0,-1e-05,130) rot=(0,0,1;0rad)
  Tip = -> Fillet005
COMPONENT P4 — recipe-attached ("RubberRing_Bottom", modeled in this document).
Construction recipe (the document's own serialized feature program — sketch geometry with constraints, then the solid features built on it; lengths are millimeters unless a unit is written):

FEATURE [Sketcher::SketchObject] Sketch017
  ArcFitTolerance = 1e-06
  AttachmentSupport = -> [XY_Plane005]
  ExternalTypes = [0]
  FullyConstrained = true
  MakeInternals = false
  MapMode = 5
  _ExternalGeoVersion = 0
  sketch-geometry (2):
    g0: Circle CenterX=0 CenterY=0 CenterZ=0 NormalX=0 NormalY=0 NormalZ=1 AngleXU=0 Radius=11
    g1: Circle CenterX=0 CenterY=0 CenterZ=0 NormalX=0 NormalY=0 NormalZ=1 AngleXU=0 Radius=10
  constraints (4):
    c: Diameter(g0) = 22
    c: Coincident(g0,g-1)
    c: Diameter(g1) = 20
    c: Coincident(g1,g0)
FEATURE [PartDesign::Pad] Pad007
  Direction = (0,0,1)
  Length = 0.75
  Length2 = 10
  Profile = -> Sketch017
  ReferenceAxis = -> Sketch017 [N_Axis]
  SideType = 0
  Suppressed = false
  Type = 0
  Type2 = 0
FEATURE [PartDesign::Fillet] Fillet006
  Base = -> Pad007 [Edge3]
  BaseFeature = -> Pad007
  Radius = 0.35
  SupportTransform = false
  Suppressed = false
  UseAllEdges = false
FEATURE [PartDesign::Fillet] Fillet007
  Base = -> Fillet006 [Edge3]
  BaseFeature = -> Fillet006
  Radius = 0.35
  SupportTransform = false
  Suppressed = false
  UseAllEdges = false
FEATURE [PartDesign::Fillet] Fillet008
  Base = -> Fillet007 [Edge9]
  BaseFeature = -> Fillet007
  Radius = 0.35
  SupportTransform = false
  Suppressed = false
  UseAllEdges = false
FEATURE [PartDesign::Fillet] Fillet009
  Base = -> Fillet008 [Edge8]
  BaseFeature = -> Fillet008
  Radius = 0.35
  SupportTransform = false
  Suppressed = false
  UseAllEdges = false
FEATURE [PartDesign::Body] Body005  label="RubberRing_Bottom"
  AllowCompound = false
  Group = -> [Sketch017,Pad007,Fillet006,Fillet007,Fillet008,Fillet009]
  Origin = -> Origin005
  Placement = pos=(0,1e-05,76.4) rot=(0,0,1;0rad)
  Tip = -> Fillet009
COMPONENT P5 — recipe-attached ("Mesh_Top", modeled in this document).
Construction recipe (the document's own serialized feature program — sketch geometry with constraints, then the solid features built on it; lengths are millimeters unless a unit is written):

FEATURE [PartDesign::SubShapeBinder] Binder
  BindCopyOnChange = 0
  BindMode = 0
  ClaimChildren = false
  Context = -> Assembly [Body006.Binder.]
  Fuse = false
  MakeFace = true
  OffsetFill = false
  OffsetIntersection = false
  OffsetJoinType = 0
  OffsetOpenResult = false
  PartialLoad = false
  Relative = true
  Support = -> [Body002[Pocket008.Edge61,Pocket008.Edge58,Pocket008.Edge62,Pocket008.Edge60,Pocket008.Edge59]]
  _Version = 2
FEATURE [PartDesign::Pad] Pad008
  Direction = (0,0,1)
  Length = 0.25
  Length2 = 10
  Profile = -> Binder
  SideType = 0
  Suppressed = false
  Type = 0
  Type2 = 0
FEATURE [PartDesign::Body] Body006  label="Mesh_Top"
  AllowCompound = false
  Group = -> [Binder,Pad008]
  Origin = -> Origin006
  Placement = pos=(0,-1e-05,54.8001) rot=(0,0,1;0rad)
  Tip = -> Pad008
COMPONENT P6 — recipe-attached ("Mesh_Bottom", modeled in this document).
Construction recipe (the document's own serialized feature program — sketch geometry with constraints, then the solid features built on it; lengths are millimeters unless a unit is written):

FEATURE [PartDesign::SubShapeBinder] Binder001
  BindCopyOnChange = 0
  BindMode = 0
  ClaimChildren = false
  Context = -> Assembly [Body007.Binder001.]
  Fuse = false
  MakeFace = true
  OffsetFill = false
  OffsetIntersection = false
  OffsetJoinType = 0
  OffsetOpenResult = false
  PartialLoad = false
  Relative = true
  Support = -> [Body[Pocket003.Edge91,Pocket003.Edge92,Pocket003.Edge94,Pocket003.Edge93]]
  _Version = 2
FEATURE [PartDesign::Pad] Pad009
  Direction = (0,0,1)
  Length = 0.1
  Length2 = 10
  Profile = -> Binder001
  SideType = 0
  Suppressed = false
  Type = 0
  Type2 = 0
FEATURE [PartDesign::Body] Body007  label="Mesh_Bottom"
  AllowCompound = false
  Group = -> [Binder001,Pad009]
  Origin = -> Origin007
  Placement = pos=(0,1e-05,110.8) rot=(0,0,1;0rad)
  Tip = -> Pad009
COMPONENT P7 — recipe-attached ("Center", modeled in this document).
Construction recipe (the document's own serialized feature program — sketch geometry with constraints, then the solid features built on it; lengths are millimeters unless a unit is written):

FEATURE [PartDesign::SubShapeBinder] Binder002
  BindCopyOnChange = 0
  BindMode = 0
  ClaimChildren = false
  Context = -> Assembly [Body008.Binder002.]
  Fuse = false
  MakeFace = true
  OffsetFill = false
  OffsetIntersection = false
  OffsetJoinType = 0
  OffsetOpenResult = false
  PartialLoad = false
  Relative = true
  Support = -> [Body002[Pocket008.Edge58,Pocket008.Edge59,Pocket008.Edge60,Pocket008.Edge62]]
  _Version = 2
FEATURE [Sketcher::SketchObject] Sketch018
  ArcFitTolerance = 1e-06
  AttachmentSupport = -> [Binder002]
  ExternalGeometry = -> [Binder002]
  ExternalTypes = [0]
  FullyConstrained = true
  MakeInternals = false
  MapMode = 5
  Placement = pos=(1.7366e-05,0,99.5) rot=(0,1.00873,0;0rad)
  _ExternalGeoVersion = 0
  sketch-geometry (4):
    g0: Circle CenterX=0 CenterY=0 CenterZ=0 NormalX=0 NormalY=0 NormalZ=1 AngleXU=0 Radius=8.9
    g1: Circle CenterX=-5.88899 CenterY=3.40002 CenterZ=0 NormalX=0 NormalY=0 NormalZ=1 AngleXU=0 Radius=1.1
    g2: Circle CenterX=5.88896 CenterY=3.40002 CenterZ=0 NormalX=0 NormalY=0 NormalZ=1 AngleXU=0 Radius=1.1
    g3: Circle CenterX=-1.5585e-05 CenterY=-6.79998 CenterZ=0 NormalX=0 NormalY=0 NormalZ=1 AngleXU=0 Radius=1.1
  constraints (8):
    c: Diameter(g0) = 17.8
    c: Coincident(g0,g-1)
    c: Coincident(g1,g-3)
    c: Equal(g1,g-3)
    c: Coincident(g2,g-4)
    c: Equal(g2,g-4)
    c: Coincident(g3,g-5)
    c: Equal(g3,g-5)
FEATURE [PartDesign::Pad] Pad010
  Direction = (1.74533e-07,0,1)
  Length = 63.9
  Length2 = 10
  Profile = -> Sketch018
  ReferenceAxis = -> Sketch018 [N_Axis]
  Reversed = true
  SideType = 0
  Suppressed = false
  Type = 0
  Type2 = 0
FEATURE [PartDesign::SubShapeBinder] Binder003  label="VentHoles_Top"
  BindCopyOnChange = 0
  BindMode = 0
  ClaimChildren = false
  Context = -> Assembly [Body008.Binder003.Edge1]
  Fuse = false
  MakeFace = true
  OffsetFill = false
  OffsetIntersection = false
  OffsetJoinType = 0
  OffsetOpenResult = false
  PartialLoad = false
  Relative = true
  Support = -> [Body002[Pocket008.Edge61,Pocket008.Edge37,Pocket008.Edge42,Pocket008.Edge41,Pocket008.Edge39,Pocket008.Edge27,Pocket008.Edge32,Pocket008.Edge29]]
  _Version = 2
FEATURE [PartDesign::SubShapeBinder] Binder004  label="VentHoles_Bottom"
  BindCopyOnChange = 0
  BindMode = 2
  ClaimChildren = false
  Context = -> Assembly [Body008.Binder004.]
  Fuse = false
  MakeFace = true
  OffsetFill = false
  OffsetIntersection = false
  OffsetJoinType = 0
  OffsetOpenResult = false
  PartialLoad = false
  Placement = pos=(0,0,-63.8) rot=(0,0,1;0rad)
  Relative = true
  _Version = 2
FEATURE [Sketcher::SketchObject] Sketch021
  ArcFitTolerance = 1e-06
  ExternalGeometry = -> [Binder004]
  ExternalTypes = [0]
  FullyConstrained = true
  MakeInternals = false
  MapMode = 5
  Placement = pos=(6.21337e-06,0,35.6) rot=(1,0,0;3.14159rad)
  _ExternalGeoVersion = 0
  sketch-geometry (14):
    g0: Circle CenterX=0 CenterY=0 CenterZ=0 NormalX=0 NormalY=0 NormalZ=1 AngleXU=0 Radius=4.09998
    g1: Circle [constr] CenterX=0 CenterY=0 CenterZ=0 NormalX=0 NormalY=0 NormalZ=1 AngleXU=0 Radius=6.70002
    g2: ArcOfCircle CenterX=-2.29154 CenterY=-6.29596 CenterZ=0 NormalX=0 NormalY=0 NormalZ=1 AngleXU=0 Radius=1.2 StartAngle=1.22173 EndAngle=4.36332
    g3: ArcOfCircle CenterX=2.29153 CenterY=-6.29596 CenterZ=0 NormalX=0 NormalY=0 NormalZ=1 AngleXU=0 Radius=1.2 StartAngle=5.06145 EndAngle=8.20305
    g4: ArcOfCircle CenterX=-4.44985e-06 CenterY=-1.5722e-05 CenterZ=0 NormalX=0 NormalY=0 NormalZ=1 AngleXU=0 Radius=5.5 StartAngle=4.36332 EndAngle=5.06145
    g5: ArcOfCircle CenterX=-4.44985e-06 CenterY=-1.6225e-05 CenterZ=0 NormalX=0 NormalY=0 NormalZ=1 AngleXU=0 Radius=7.9 StartAngle=4.36332 EndAngle=5.06145
    g6: ArcOfCircle CenterX=-4.44985e-06 CenterY=-1.5722e-05 CenterZ=0 NormalX=0 NormalY=0 NormalZ=1 AngleXU=0 Radius=5.5 StartAngle=0.174533 EndAngle=0.872665
    g7: ArcOfCircle CenterX=-4.44985e-06 CenterY=-1.5722e-05 CenterZ=0 NormalX=0 NormalY=0 NormalZ=1 AngleXU=0 Radius=7.9 StartAngle=0.174533 EndAngle=0.872665
    g8: ArcOfCircle CenterX=4.30667 CenterY=5.13248 CenterZ=0 NormalX=0 NormalY=0 NormalZ=1 AngleXU=0 Radius=1.2 StartAngle=0.872665 EndAngle=4.01426
    g9: ArcOfCircle CenterX=6.59821 CenterY=1.16343 CenterZ=0 NormalX=0 NormalY=0 NormalZ=1 AngleXU=0 Radius=1.2 StartAngle=3.31613 EndAngle=6.45771
    g10: ArcOfCircle CenterX=-4.30668 CenterY=5.13248 CenterZ=0 NormalX=0 NormalY=0 NormalZ=1 AngleXU=0 Radius=1.2 StartAngle=5.41052 EndAngle=8.55211
    g11: ArcOfCircle CenterX=-6.59822 CenterY=1.16343 CenterZ=0 NormalX=0 NormalY=0 NormalZ=1 AngleXU=0 Radius=1.2 StartAngle=2.96706 EndAngle=6.10865
    g12: ArcOfCircle CenterX=-5.36395e-06 CenterY=-1.51943e-05 CenterZ=0 NormalX=0 NormalY=0 NormalZ=1 AngleXU=0 Radius=5.5 StartAngle=2.26893 EndAngle=2.96706
    g13: ArcOfCircle CenterX=-4.22077e-06 CenterY=-1.58543e-05 CenterZ=0 NormalX=0 NormalY=0 NormalZ=1 AngleXU=0 Radius=7.9 StartAngle=2.26893 EndAngle=2.96706
  constraints (34):
    c: Coincident(g0,g-1)
    c: Tangent(g0,g-3)
    c: Coincident(g1,g0)
    c: PointOnObject(g-5,g1)
    c: Coincident(g2,g-6)
    c: Coincident(g2,g-8)
    c: Tangent(g2,g-5)
    c: Tangent(g3,g-18) = -1.5708
    c: Coincident(g3,g-18)
    c: Tangent(g4,g-6) = -1.5708
    c: Coincident(g4,g-18)
    c: Coincident(g5,g2)
    c: Coincident(g5,g3)
    c: Tangent(g5,g-8)
    c: Tangent(g6,g-17) = -1.5708
    c: Coincident(g6,g-17)
    c: Tangent(g7,g-15) = -1.5708
    c: Coincident(g7,g-16)
    c: Coincident(g8,g6)
    c: Coincident(g8,g7)
    c: Tangent(g8,g-14)
    c: Coincident(g9,g6)
    c: Coincident(g9,g7)
    c: Tangent(g9,g-16)
    c: Tangent(g10,g-12) = -1.5708
    c: Coincident(g10,g-12)
    c: Tangent(g11,g-11) = -1.5708
    c: Coincident(g11,g-11)
    c: Coincident(g12,g11)
    c: Coincident(g12,g-12)
    c: Tangent(g12,g-9)
    c: Coincident(g13,g10)
    c: Coincident(g13,g11)
    c: Tangent(g13,g-10)
FEATURE [PartDesign::Pocket] Pocket011  label="VentHoles_Bottom_Pocket"
  BaseFeature = -> Pad010
  Direction = (1.74533e-07,1e-16,1)
  Length = 5
  Length2 = 5
  Profile = -> Sketch021
  ReferenceAxis = -> Sketch021 [N_Axis]
  SideType = 0
  Suppressed = false
  Type = 0
  Type2 = 0
FEATURE [Sketcher::SketchObject] Sketch022
  ArcFitTolerance = 1e-06
  AttachmentSupport = -> [Pocket011]
  ExternalGeometry = -> [Binder003]
  ExternalTypes = [0]
  FullyConstrained = true
  MakeInternals = false
  MapMode = 5
  Placement = pos=(1.7366e-05,0,99.5) rot=(0,1.00873,0;0rad)
  _ExternalGeoVersion = 0
  sketch-geometry (13):
    g0: Circle CenterX=0 CenterY=0 CenterZ=0 NormalX=0 NormalY=0 NormalZ=1 AngleXU=0 Radius=4.10002
    g1: ArcOfCircle CenterX=-4.30669 CenterY=-5.13248 CenterZ=0 NormalX=0 NormalY=0 NormalZ=1 AngleXU=0 Radius=1.2 StartAngle=4.01426 EndAngle=7.15585
    g2: ArcOfCircle CenterX=-6.59823 CenterY=-1.16343 CenterZ=0 NormalX=0 NormalY=0 NormalZ=1 AngleXU=0 Radius=1.2 StartAngle=0.174533 EndAngle=3.31613
    g3: ArcOfCircle CenterX=-1.49833e-05 CenterY=1.60694e-05 CenterZ=0 NormalX=0 NormalY=0 NormalZ=1 AngleXU=0 Radius=5.5 StartAngle=3.31613 EndAngle=4.01426
    g4: ArcOfCircle CenterX=-1.60752e-05 CenterY=1.54391e-05 CenterZ=0 NormalX=0 NormalY=0 NormalZ=1 AngleXU=0 Radius=7.9 StartAngle=3.31613 EndAngle=4.01426
    g5: ArcOfCircle CenterX=-1.5585e-05 CenterY=1.5722e-05 CenterZ=0 NormalX=0 NormalY=0 NormalZ=1 AngleXU=0 Radius=5.5 StartAngle=5.41052 EndAngle=6.10865
    g6: ArcOfCircle CenterX=-1.5585e-05 CenterY=1.5722e-05 CenterZ=0 NormalX=0 NormalY=0 NormalZ=1 AngleXU=0 Radius=7.9 StartAngle=5.41052 EndAngle=6.10865
    g7: ArcOfCircle CenterX=4.30666 CenterY=-5.13248 CenterZ=0 NormalX=0 NormalY=0 NormalZ=1 AngleXU=0 Radius=1.2 StartAngle=2.26893 EndAngle=5.41052
    g8: ArcOfCircle CenterX=6.5982 CenterY=-1.16342 CenterZ=0 NormalX=0 NormalY=0 NormalZ=1 AngleXU=0 Radius=1.2 StartAngle=6.10865 EndAngle=9.25025
    g9: ArcOfCircle CenterX=2.29152 CenterY=6.29596 CenterZ=0 NormalX=0 NormalY=0 NormalZ=1 AngleXU=0 Radius=1.2 StartAngle=4.36332 EndAngle=7.50492
    g10: ArcOfCircle CenterX=-2.29155 CenterY=6.29596 CenterZ=0 NormalX=0 NormalY=0 NormalZ=1 AngleXU=0 Radius=1.2 StartAngle=1.91986 EndAngle=5.06145
    g11: ArcOfCircle CenterX=-1.5585e-05 CenterY=1.95751e-05 CenterZ=0 NormalX=0 NormalY=0 NormalZ=1 AngleXU=0 Radius=5.5 StartAngle=1.22173 EndAngle=1.91986
    g12: ArcOfCircle CenterX=-1.5585e-05 CenterY=1.61708e-05 CenterZ=0 NormalX=0 NormalY=0 NormalZ=1 AngleXU=0 Radius=7.9 StartAngle=1.22173 EndAngle=1.91986
  constraints (34):
    c: Coincident(g0,g-1)
    c: Tangent(g0,g-15)
    c: Tangent(g1,g-5) = -1.5708
    c: Coincident(g1,g-5)
    c: Tangent(g2,g-6) = -1.5708
    c: Coincident(g2,g-6)
    c: Coincident(g3,g1)
    c: Coincident(g3,g-6)
    c: Tangent(g3,g-3)
    c: Coincident(g4,g1)
    c: Coincident(g4,g2)
    c: Tangent(g4,g-4)
    c: Coincident(g5,g-13)
    c: Coincident(g5,g-14)
    c: Tangent(g5,g-12)
    c: Coincident(g6,g-13)
    c: Coincident(g6,g-14)
    c: Tangent(g6,g-11)
    c: Coincident(g7,g6)
    c: Coincident(g7,g5)
    c: Tangent(g7,g-14)
    c: Coincident(g8,g6)
    c: Coincident(g8,g5)
    c: Tangent(g8,g-13)
    c: Coincident(g9,g-10)
    c: Tangent(g9,g-9) = -1.5708
    c: Coincident(g10,g-10)
    c: Tangent(g10,g-8) = -1.5708
    c: Coincident(g11,g10)
    c: Coincident(g11,g9)
    c: Tangent(g11,g-7)
    c: Coincident(g12,g10)
    c: Coincident(g12,g9)
    c: Tangent(g12,g-10)
FEATURE [PartDesign::Pocket] Pocket012  label="Ventholes_Top_Pocket"
  BaseFeature = -> Pocket011
  Direction = (-1.74533e-07,0,-1)
  Length = 5
  Length2 = 5
  Profile = -> Sketch022
  ReferenceAxis = -> Sketch022 [N_Axis]
  SideType = 0
  Suppressed = false
  Type = 0
  Type2 = 0
FEATURE [PartDesign::Plane] DatumPlane
  AttachmentOffset = pos=(0,0,0) rot=(1,0,0;1.5708rad)
  AttachmentSupport = -> [Pocket012]
  Length = 65.7798
  MapMode = 5
  Placement = pos=(1.7366e-05,0,99.5) rot=(1.00436,0,0;1.5708rad)
  ResizeMode = 0
  Width = 140.28
FEATURE [Sketcher::SketchObject] Sketch023
  ArcFitTolerance = 1e-06
  AttachmentSupport = -> [DatumPlane]
  ExternalGeometry = -> [Pocket012]
  ExternalTypes = [0]
  FullyConstrained = true
  MakeInternals = false
  MapMode = 5
  Placement = pos=(1.7366e-05,0,99.5) rot=(1,0,0;1.5708rad)
  _ExternalGeoVersion = 0
  sketch-geometry (8):
    g0: GeomPoint X=8.9 Y=-58.9 Z=0
    g1: GeomPoint X=8.9 Y=-5 Z=0
    g2: GeomPoint X=-8.9 Y=-5 Z=0
    g3: GeomPoint X=-8.9 Y=-58.9 Z=0
    g4: LineSegment StartX=-8.9 StartY=-5 StartZ=0 EndX=-8.9 EndY=-58.9 EndZ=0
    g5: LineSegment StartX=-8.9 StartY=-58.9 StartZ=0 EndX=8.9 EndY=-58.9 EndZ=0
    g6: LineSegment StartX=8.9 StartY=-58.9 StartZ=0 EndX=8.9 EndY=-5 EndZ=0
    g7: LineSegment StartX=8.9 StartY=-5 StartZ=0 EndX=-8.9 EndY=-5 EndZ=0
  constraints (18):
    c: PointOnObject(g0,g-3)
    c: PointOnObject(g1,g-3)
    c: DistanceY(g1,g-3) = 5
    c: DistanceY(g-4,g0) = 5
    c: DistanceX(g3,g0) = 17.8
    c: DistanceX(g2,g1) = 17.8
    c: DistanceY(g3,g0) = 0
    c: DistanceY(g2,g1) = 0
    c: Coincident(g4,g5)
    c: Coincident(g5,g6)
    c: Coincident(g6,g7)
    c: Coincident(g7,g4)
    c: Vertical(g4)
    c: Vertical(g6)
    c: Horizontal(g5)
    c: Horizontal(g7)
    c: Coincident(g4,g2)
    c: Coincident(g5,g0)
FEATURE [PartDesign::Pocket] Pocket013  label="CenterCutout"
  BaseFeature = -> Pocket012
  Direction = (0,1,-1e-16)
  Length = 5
  Length2 = 5
  Profile = -> Sketch023
  ReferenceAxis = -> Sketch023 [N_Axis]
  Reversed = true
  SideType = 0
  Suppressed = false
  Type = 1
  Type2 = 0
FEATURE [Sketcher::SketchObject] Sketch024  label="BacksideChannel"
  ArcFitTolerance = 1e-06
  AttachmentOffset = pos=(0,0,-5) rot=(0,0,1;0rad)
  AttachmentSupport = -> [Pocket013]
  ExternalGeometry = -> [Pocket013]
  ExternalTypes = [0]
  FullyConstrained = true
  MakeInternals = false
  MapMode = 5
  Placement = pos=(1.64934e-05,0,94.5) rot=(0,1.00873,0;0rad)
  _ExternalGeoVersion = 0
  sketch-geometry (10):
    g0: LineSegment [constr] StartX=-2.29155 StartY=6.29596 StartZ=0 EndX=-12.2916 EndY=6.29596 EndZ=0
    g1: LineSegment [constr] StartX=-2.29155 StartY=6.29596 StartZ=0 EndX=17.7084 EndY=6.29596 EndZ=0
    g2: ArcOfCircle CenterX=-2.29155 CenterY=6.29596 CenterZ=0 NormalX=0 NormalY=0 NormalZ=1 AngleXU=0 Radius=1.2 StartAngle=3.14159 EndAngle=5.06145
    g3: ArcOfCircle CenterX=2.29152 CenterY=6.29596 CenterZ=0 NormalX=0 NormalY=0 NormalZ=1 AngleXU=0 Radius=1.2 StartAngle=4.36332 EndAngle=6.28319
    g4: GeomPoint X=-6.29054 Y=6.29596 Z=0
    g5: GeomPoint X=6.29054 Y=6.29596 Z=0
    g6: LineSegment StartX=-3.49155 StartY=6.29596 StartZ=0 EndX=-6.29054 EndY=6.29596 EndZ=0
    g7: LineSegment StartX=3.49152 StartY=6.29596 StartZ=0 EndX=6.29054 EndY=6.29596 EndZ=0
    g8: ArcOfCircle CenterX=5.72e-14 CenterY=0 CenterZ=0 NormalX=0 NormalY=0 NormalZ=1 AngleXU=0 Radius=8.9 StartAngle=0.785828 EndAngle=2.35576
    g9: ArcOfCircle CenterX=-1.5585e-05 CenterY=2.11004e-05 CenterZ=0 NormalX=0 NormalY=0 NormalZ=1 AngleXU=0 Radius=5.49999 StartAngle=1.22173 EndAngle=1.91986
  constraints (26):
    c: Distance(g0) = 10
    c: Horizontal(g0)
    c: Coincident(g0,g-5)
    c: Distance(g1) = 20
    c: Coincident(g1,g0)
    c: Horizontal(g1)
    c: Coincident(g2,g0)
    c: Coincident(g2,g-5)
    c: PointOnObject(g2,g0)
    c: Coincident(g3,g-6)
    c: Coincident(g3,g-6)
    c: PointOnObject(g3,g1)
    c: PointOnObject(g4,g-3)
    c: PointOnObject(g5,g-3)
    c: PointOnObject(g5,g1)
    c: PointOnObject(g4,g0)
    c: Coincident(g6,g2)
    c: Coincident(g6,g4)
    c: Coincident(g7,g3)
    c: Coincident(g7,g5)
    c: Coincident(g8,g4)
    c: Coincident(g8,g5)
    c: PointOnObject(g8,g-1)
    c: Coincident(g9,g2)
    c: Coincident(g9,g3)
    c: Tangent(g9,g-4)
FEATURE [PartDesign::Pocket] Pocket014  label="VentilationChannel"
  BaseFeature = -> Pocket013
  Direction = (-1.74533e-07,0,-1)
  Length = 45
  Length2 = 5
  Profile = -> Sketch024
  ReferenceAxis = -> Sketch024 [N_Axis]
  SideType = 0
  Suppressed = false
  Type = 2
  Type2 = 0
FEATURE [Sketcher::SketchObject] Sketch025  label="PCBcutout"
  ArcFitTolerance = 1e-06
  AttachmentSupport = -> [Pocket014]
  ExternalGeometry = -> [Pocket014]
  ExternalTypes = [0]
  FullyConstrained = false
  MakeInternals = false
  MapMode = 5
  Placement = pos=(0,0,0) rot=(1,0,0;1.5708rad)
  _ExternalGeoVersion = 0
  sketch-geometry (23):
    g0: LineSegment [constr] StartX=-7.5 StartY=91.3 StartZ=0 EndX=-7.5 EndY=41.3 EndZ=0
    g1: LineSegment [constr] StartX=-7.5 StartY=41.3 StartZ=0 EndX=7.5 EndY=41.3 EndZ=0
    g2: LineSegment [constr] StartX=7.5 StartY=41.3 StartZ=0 EndX=7.5 EndY=91.3 EndZ=0
    g3: LineSegment [constr] StartX=7.5 StartY=91.3 StartZ=0 EndX=-7.5 EndY=91.3 EndZ=0
    g4: GeomPoint X=-7.7 Y=91.5 Z=0
    g5: GeomPoint X=7.7 Y=41.1 Z=0
    g6: LineSegment [constr] StartX=-7.7 StartY=91.5 StartZ=0 EndX=-7.7 EndY=41.1 EndZ=0
    g7: LineSegment StartX=-7.7 StartY=41.1 StartZ=0 EndX=7.7 EndY=41.1 EndZ=0
    g8: LineSegment [constr] StartX=7.7 StartY=41.1 StartZ=0 EndX=7.7 EndY=91.5 EndZ=0
    g9: LineSegment StartX=7.7 StartY=91.5 StartZ=0 EndX=-7.7 EndY=91.5 EndZ=0
    g10: ArcOfCircle CenterX=-7.7 CenterY=45.8 CenterZ=0 NormalX=0 NormalY=0 NormalZ=1 AngleXU=0 Radius=1.5 StartAngle=4.71239 EndAngle=7.85398
    g11: LineSegment StartX=-7.7 StartY=41.1 StartZ=0 EndX=-7.7 EndY=44.3 EndZ=0
    g12: GeomPoint X=7.7 Y=45.8 Z=0
    g13: ArcOfCircle CenterX=7.7 CenterY=45.8 CenterZ=0 NormalX=0 NormalY=0 NormalZ=1 AngleXU=0 Radius=1.5 StartAngle=1.5708 EndAngle=4.71239
    g14: LineSegment StartX=7.7 StartY=44.3 StartZ=0 EndX=7.7 EndY=41.1 EndZ=0
    g15: GeomPoint X=-7.7 Y=85.8 Z=0
    g16: ArcOfCircle CenterX=-7.7 CenterY=85.8 CenterZ=0 NormalX=0 NormalY=0 NormalZ=1 AngleXU=0 Radius=1.5 StartAngle=4.71239 EndAngle=7.85398
    g17: LineSegment StartX=-7.7 StartY=84.3 StartZ=0 EndX=-7.7 EndY=47.3 EndZ=0
    g18: LineSegment StartX=-7.7 StartY=87.3 StartZ=0 EndX=-7.7 EndY=91.5 EndZ=0
    g19: GeomPoint X=7.7 Y=85.8 Z=0
    g20: ArcOfCircle CenterX=7.7 CenterY=85.8 CenterZ=0 NormalX=0 NormalY=0 NormalZ=1 AngleXU=0 Radius=1.5 StartAngle=1.5708 EndAngle=4.71239
    g21: LineSegment StartX=7.7 StartY=87.3 StartZ=0 EndX=7.7 EndY=91.5 EndZ=0
    g22: LineSegment StartX=7.7 StartY=84.3 StartZ=0 EndX=7.7 EndY=47.3 EndZ=0
  constraints (60):
    c: Coincident(g0,g1)
    c: Coincident(g1,g2)
    c: Coincident(g2,g3)
    c: Coincident(g3,g0)
    c: Vertical(g0)
    c: Vertical(g2)
    c: Horizontal(g1)
    c: Horizontal(g3)
    c: DistanceX(g0,g2) = 15
    c: DistanceY(g0,g0) = 50
    c: DistanceX(g0,g-1) = 7.5
    c: DistanceX(g1,g5) = 0.2
    c: DistanceX(g4,g0) = 0.2
    c: DistanceY(g0,g4) = 0.2
    c: DistanceY(g5,g1) = 0.2
    c: Coincident(g6,g7)
    c: Coincident(g7,g8)
    c: Coincident(g8,g9)
    c: Coincident(g9,g6)
    c: Vertical(g6)
    c: Vertical(g8)
    c: Horizontal(g7)
    c: Horizontal(g9)
    c: Coincident(g6,g4)
    c: Coincident(g7,g5)
    c: PointOnObject(g10,g6)
    c: PointOnObject(g10,g6)
    c: PointOnObject(g10,g6)
    c: Radius(g10) = 1.5
    c: DistanceY(g0,g10) = 4.5
    c: DistanceY(g11,g0) = 0.2
    c: DistanceX(g11,g0) = 0.2
    c: PointOnObject(g12,g8)
    c: DistanceY(g10,g12) = 0
    c: Coincident(g13,g12)
    c: PointOnObject(g13,g8)
    c: PointOnObject(g13,g8)
    c: Radius(g13) = 1.5
    c: Coincident(g14,g13)
    c: Coincident(g14,g5)
    c: Coincident(g11,g10)
    c: DistanceY(g15,g0) = 5.5
    c: Coincident(g16,g15)
    c: Radius(g16) = 1.5
    c: Coincident(g17,g16)
    c: Coincident(g17,g10)
    c: Vertical(g17)
    c: Coincident(g18,g16)
    c: Coincident(g18,g4)
    c: Vertical(g18)
    c: DistanceY(g15,g19) = 0
    c: Coincident(g20,g19)
    c: Radius(g20) = 1.5
    c: Coincident(g21,g20)
    c: Coincident(g21,g8)
    c: Vertical(g21)
    c: Coincident(g22,g20)
    c: Coincident(g22,g13)
    c: Vertical(g22)
    c: DistanceY(g-6,g0) = 0.7
FEATURE [Sketcher::SketchObject] Sketch026  label="BMEcutout"
  ArcFitTolerance = 1e-06
  AttachmentSupport = -> [Pocket014]
  ExternalGeometry = -> [Pocket014]
  ExternalTypes = [0]
  FullyConstrained = true
  MakeInternals = false
  MapMode = 5
  Placement = pos=(7.08603e-06,0,40.6) rot=(1,0,0;3.14159rad)
  _ExternalGeoVersion = 0
  sketch-geometry (2):
    g0: ArcOfCircle CenterX=3.3e-15 CenterY=0 CenterZ=0 NormalX=0 NormalY=0 NormalZ=1 AngleXU=0 Radius=4.09998 StartAngle=3.14159 EndAngle=6.28319
    g1: LineSegment StartX=-4.09998 StartY=5e-16 StartZ=0 EndX=4.09998 EndY=-1e-15 EndZ=0
  constraints (4):
    c: Tangent(g0,g-3) = -1.5708
    c: Coincident(g0,g-3)
    c: Coincident(g1,g0)
    c: Coincident(g1,g0)
FEATURE [PartDesign::Pocket] Pocket015  label="BMEcutoutPocket"
  BaseFeature = -> Pocket014
  Direction = (1.74533e-07,0,1)
  Length = 7.5
  Length2 = 5
  Profile = -> Sketch026
  ReferenceAxis = -> Sketch026 [N_Axis]
  SideType = 0
  Suppressed = false
  Type = 0
  Type2 = 0
FEATURE [PartDesign::Pocket] Pocket016  label="PCBcutoutPocket"
  BaseFeature = -> Pocket015
  Direction = (0,1,-2e-16)
  Length = 0.7
  Length2 = 5
  Profile = -> Sketch025
  ReferenceAxis = -> Sketch025 [N_Axis]
  SideType = 0
  Suppressed = false
  Type = 0
  Type2 = 0
FEATURE [PartDesign::Body] Body008  label="Center"
  AllowCompound = false
  Group = -> [Binder002,Sketch018,Pad010,Binder003,Binder004,Sketch021,Pocket011,Sketch022,Pocket012,DatumPlane,Sketch023,Pocket013,Sketch024,Pocket014,Sketch025,Sketch026,Pocket015,Pocket016]
  Origin = -> Origin009
  Placement = pos=(0,-5.72205e-06,36.0001) rot=(0,0,1;0rad)
  Tip = -> Pocket016
COMPONENT P8 — recipe-attached ("CableProtector", modeled in this document).
Construction recipe (the document's own serialized feature program — sketch geometry with constraints, then the solid features built on it; lengths are millimeters unless a unit is written):

FEATURE [PartDesign::Plane] DatumPlane001
  AttachmentOffset = pos=(0,-80,-2) rot=(0,0,1;0rad)
  AttachmentSupport = -> [Pocket016]
  Length = 69.3866
  MapMode = 45
  Placement = pos=(2.57523e-05,-0.0934557,147.55) rot=(-1,0,0;1.5708rad)
  ResizeMode = 0
  Width = 207.307
FEATURE [Sketcher::SketchObject] Sketch027
  ArcFitTolerance = 1e-06
  AttachmentSupport = -> [DatumPlane001]
  ExternalTypes = [0]
  FullyConstrained = true
  MakeInternals = false
  MapMode = 5
  Placement = pos=(2.57523e-05,-0.0934557,147.55) rot=(-1,0,0;1.5708rad)
  _ExternalGeoVersion = 0
  sketch-geometry (23):
    g0: LineSegment StartX=-5.2 StartY=7.35 StartZ=0 EndX=-3.2 EndY=7.35 EndZ=0
    g1: LineSegment StartX=-3.2 StartY=9.85 StartZ=0 EndX=-3.2 EndY=7.35 EndZ=0
    g2: LineSegment StartX=-3.2 StartY=9.85 StartZ=0 EndX=-4 EndY=9.85 EndZ=0
    g3: LineSegment StartX=-4 StartY=9.85 StartZ=0 EndX=-4 EndY=11.63 EndZ=0
    g4: LineSegment StartX=-2 StartY=11.63 StartZ=0 EndX=-2 EndY=-15.37 EndZ=0
    g5: LineSegment StartX=-4 StartY=11.63 StartZ=0 EndX=-2 EndY=11.63 EndZ=0
    g6: LineSegment StartX=-5.2 StartY=7.35 StartZ=0 EndX=-5.2 EndY=4.85 EndZ=0
    g7: LineSegment StartX=-2.7 StartY=0.85 StartZ=0 EndX=-3.5 EndY=0.85 EndZ=0
    g8: LineSegment StartX=-2.7 StartY=2.85 StartZ=0 EndX=-2.7 EndY=0.85 EndZ=0
    g9: LineSegment StartX=-3.5 StartY=0.85 StartZ=0 EndX=-3.5 EndY=-3.15 EndZ=0
    g10: LineSegment StartX=-2.7 StartY=-3.37 StartZ=0 EndX=-2.7 EndY=-5.37 EndZ=0
    g11: LineSegment StartX=-2.7 StartY=-5.37 StartZ=0 EndX=-3.5 EndY=-5.37 EndZ=0
    g12: LineSegment StartX=-3.5 StartY=-9.37 StartZ=0 EndX=-2.7 EndY=-9.37 EndZ=0
    g13: LineSegment StartX=-2.7 StartY=-9.37 StartZ=0 EndX=-2.7 EndY=-11.37 EndZ=0
    g14: LineSegment StartX=-2.7 StartY=-11.37 StartZ=0 EndX=-3.5 EndY=-11.37 EndZ=0
    g15: LineSegment StartX=-3.5 StartY=-11.37 StartZ=0 EndX=-3.5 EndY=-15.37 EndZ=0
    g16: LineSegment StartX=-3.5 StartY=-15.37 StartZ=0 EndX=-2 EndY=-15.37 EndZ=0
    g17: LineSegment StartX=-3.5 StartY=2.85 StartZ=0 EndX=-2.7 EndY=2.85 EndZ=0
    g18: LineSegment StartX=-5.2 StartY=4.85 StartZ=0 EndX=-4.35 EndY=4.85 EndZ=0
    g19: ArcOfCircle CenterX=-4.66305 CenterY=3.72266 CenterZ=0 NormalX=0 NormalY=0 NormalZ=1 AngleXU=0 Radius=1.17 StartAngle=0.109055 EndAngle=1.29993
    g20: LineSegment StartX=-3.5 StartY=3.85 StartZ=0 EndX=-3.5 EndY=2.85 EndZ=0
    g21: LineSegment StartX=-3.5 StartY=-5.37 StartZ=0 EndX=-3.5 EndY=-9.37 EndZ=0
    g22: LineSegment StartX=-3.5 StartY=-3.15 StartZ=0 EndX=-2.7 EndY=-3.37 EndZ=0
  constraints (70):
    c: Coincident(g18,g19)
    c: DistanceX(g16,g-1) = 2
    c: Coincident(g4,g16)
    c: DistanceX(g16,g16) = 1.5
    c: DistanceY(g16,g4) = 0
    c: Coincident(g15,g16)
    c: DistanceX(g14,g14) = 0.8
    c: DistanceY(g15,g15) = 4
    c: DistanceY(g14,g14) = 0
    c: DistanceX(g15,g15) = 0
    c: Coincident(g14,g15)
    c: Coincident(g13,g14)
    c: DistanceY(g13,g13) = 2
    c: DistanceX(g12,g13) = 0
    c: Coincident(g12,g13)
    c: DistanceX(g12,g12) = 0.8
    c: DistanceY(g12,g12) = 0
    c: DistanceY(g4,g4) = 27
    c: Coincident(g21,g11)
    c: Coincident(g21,g12)
    c: Vertical(g21)
    c: DistanceY(g21,g21) = 4
    c: DistanceY(g11,g10) = 0
    c: DistanceX(g11,g10) = 0.8
    c: Coincident(g11,g10)
    c: DistanceY(g10,g10) = 2
    c: DistanceX(g10,g10) = 0
    c: DistanceY(g4,g-1) = 15.37
    c: DistanceX(g4,g4) = 0
    c: DistanceY(g5,g5) = 0
    c: Coincident(g5,g4)
    c: DistanceX(g5,g5) = 2
    c: Coincident(g3,g5)
    c: DistanceY(g3,g3) = 1.78
    c: DistanceX(g3,g4) = 2
    c: Coincident(g2,g3)
    c: DistanceX(g2,g2) = 0.8
    c: DistanceY(g2,g2) = 0
    c: Coincident(g1,g2)
    c: DistanceY(g1,g1) = 2.5
    c: DistanceX(g1,g1) = 0
    c: Coincident(g0,g1)
    c: DistanceX(g0,g0) = 2
    c: DistanceY(g0,g0) = 0
    c: Coincident(g6,g0)
    c: DistanceY(g6,g6) = 2.5
    c: Coincident(g6,g18)
    c: DistanceX(g6,g0) = 0
    c: DistanceX(g18,g18) = 0.85
    c: DistanceY(g6,g18) = 0
    c: DistanceX(g19,g0) = 0.3
    c: DistanceY(g19,g18) = 1
    c: Radius(g19) = 1.17
    c: Coincident(g20,g19)
    c: DistanceY(g20,g20) = 1
    c: DistanceX(g19,g17) = 0
    c: Coincident(g17,g20)
    c: DistanceY(g8,g8) = 2
    c: DistanceY(g17,g8) = 0
    c: DistanceX(g17,g8) = 0.8
    c: Coincident(g17,g8)
    c: DistanceX(g8,g8) = 0
    c: Coincident(g7,g8)
    c: DistanceX(g7,g7) = 0.8
    c: DistanceY(g7,g7) = 0
    c: Coincident(g9,g7)
    c: DistanceY(g9,g9) = 4
    c: DistanceX(g7,g9) = 0
    c: Coincident(g22,g9)
    c: Coincident(g22,g10)
FEATURE [PartDesign::Revolution] Revolution
  Angle = 360
  Angle2 = 60
  Axis = (-1.74533e-07,3e-16,-1)
  Base = (2.57523e-05,-0.0934557,147.55)
  FuseOrder = 1
  Placement = pos=(2.57523e-05,-0.0934557,147.55) rot=(-1,0,0;1.5708rad)
  Profile = -> Sketch027
  ReferenceAxis = -> Sketch027 [V_Axis]
  Suppressed = false
  Type = 0
FEATURE [PartDesign::Body] Body009  label="CableProtector"
  AllowCompound = false
  Group = -> [DatumPlane001,Sketch027,Revolution]
  Origin = -> Origin010
  Placement = pos=(0,0,-1.4) rot=(0,0,1;0rad)
  Tip = -> Revolution
COMPONENT P9 — recipe-attached ("MeshMask_Top", modeled in this document).
Construction recipe (the document's own serialized feature program — sketch geometry with constraints, then the solid features built on it; lengths are millimeters unless a unit is written):

FEATURE [PartDesign::SubShapeBinder] Binder006
  BindCopyOnChange = 0
  BindMode = 0
  ClaimChildren = false
  Context = -> Assembly [Body012.Binder006.]
  Fuse = false
  MakeFace = true
  OffsetFill = false
  OffsetIntersection = false
  OffsetJoinType = 0
  OffsetOpenResult = false
  PartialLoad = false
  Relative = true
  Support = -> [Body011[Pocket023.Edge61,Pocket023.Edge58,Pocket023.Edge62,Pocket023.Edge60,Pocket023.Edge59]]
  _Version = 2
FEATURE [PartDesign::SubShapeBinder] Binder007
  BindCopyOnChange = 0
  BindMode = 0
  ClaimChildren = false
  Context = -> Assembly [Body012.Binder007.]
  Fuse = false
  MakeFace = true
  OffsetFill = false
  OffsetIntersection = false
  OffsetJoinType = 0
  OffsetOpenResult = false
  PartialLoad = false
  Refine = true
  Relative = true
  Support = -> [Body011[Pocket023.Edge51,Pocket023.Edge56,Pocket023.Edge55,Pocket023.Edge53,Pocket023.Edge42,Pocket023.Edge37,Pocket023.Edge39,Pocket023.Edge41]]
  _Version = 2
FEATURE [PartDesign::Pad] Pad013
  Direction = (1.74533e-07,0,1)
  Length = 0.25
  Length2 = 10
  Profile = -> Binder006
  SideType = 0
  Suppressed = false
  Type = 0
  Type2 = 0
FEATURE [PartDesign::Pocket] Pocket024
  BaseFeature = -> Pad013
  Direction = (-1.74533e-07,0,-1)
  Length = 5
  Length2 = 5
  Profile = -> Binder007
  Reversed = true
  SideType = 0
  Suppressed = false
  Type = 1
  Type2 = 0
FEATURE [PartDesign::Body] Body012  label="MeshMask_Top"
  AllowCompound = false
  Group = -> [Binder006,Pad013,Binder007,Pocket024]
  Origin = -> Origin024
  Placement = pos=(0,0,53.8) rot=(0,0,1;0rad)
  Tip = -> Pocket024
COMPONENT P10 — recipe-attached ("MeshMask_Bottom", modeled in this document).
Construction recipe (the document's own serialized feature program — sketch geometry with constraints, then the solid features built on it; lengths are millimeters unless a unit is written):

FEATURE [PartDesign::SubShapeBinder] Binder008
  BindCopyOnChange = 0
  BindMode = 0
  ClaimChildren = false
  Context = -> Assembly [Body014.Binder008.]
  Fuse = false
  MakeFace = true
  OffsetFill = false
  OffsetIntersection = false
  OffsetJoinType = 0
  OffsetOpenResult = false
  PartialLoad = false
  Relative = true
  Support = -> [Body013[Pocket029.Edge61,Pocket029.Edge58,Pocket029.Edge62,Pocket029.Edge60,Pocket029.Edge59]]
  _Version = 2
FEATURE [PartDesign::SubShapeBinder] Binder009
  BindCopyOnChange = 0
  BindMode = 0
  ClaimChildren = false
  Context = -> Assembly [Body014.Binder009.]
  Fuse = false
  MakeFace = true
  OffsetFill = false
  OffsetIntersection = false
  OffsetJoinType = 0
  OffsetOpenResult = false
  PartialLoad = false
  Refine = true
  Relative = true
  Support = -> [Body013[Pocket029.Edge51,Pocket029.Edge56,Pocket029.Edge55,Pocket029.Edge53,Pocket029.Edge42,Pocket029.Edge37,Pocket029.Edge39,Pocket029.Edge41]]
  _Version = 2
FEATURE [PartDesign::Pad] Pad016
  Direction = (1.74533e-07,-4e-16,1)
  Length = 0.25
  Length2 = 10
  Profile = -> Binder008
  SideType = 0
  Suppressed = false
  Type = 0
  Type2 = 0
FEATURE [PartDesign::Pocket] Pocket030
  BaseFeature = -> Pad016
  Direction = (-1.74533e-07,0,-1)
  Length = 5
  Length2 = 5
  Profile = -> Binder009
  Reversed = true
  SideType = 0
  Suppressed = false
  Type = 1
  Type2 = 0
FEATURE [PartDesign::Body] Body014  label="MeshMask_Bottom"
  AllowCompound = false
  Group = -> [Binder008,Pad016,Binder009,Pocket030]
  Origin = -> Origin028
  Placement = pos=(0,0,-214.8) rot=(0,0,1;0rad)
  Tip = -> Pocket030
COMPONENT P11 — recipe-attached ("HexBolt_Bottom_1", modeled in this document).
Construction recipe (the document's own serialized feature program — sketch geometry with constraints, then the solid features built on it; lengths are millimeters unless a unit is written):

FEATURE [Sketcher::SketchObject] Sketch028
  ArcFitTolerance = 1e-06
  AttachmentSupport = -> [XZ_Plane011]
  ExternalTypes = [0]
  FullyConstrained = true
  MakeInternals = false
  MapMode = 5
  Placement = pos=(0,0,0) rot=(1,0,0;1.5708rad)
  _ExternalGeoVersion = 0
  sketch-geometry (6):
    g0: LineSegment StartX=0 StartY=0 StartZ=0 EndX=0 EndY=7 EndZ=0
    g1: LineSegment StartX=0 StartY=7 StartZ=0 EndX=1 EndY=7 EndZ=0
    g2: LineSegment StartX=1 StartY=7 StartZ=0 EndX=1 EndY=1.5 EndZ=0
    g3: LineSegment StartX=1 StartY=1.5 StartZ=0 EndX=1.9 EndY=1.5 EndZ=0
    g4: LineSegment StartX=1.9 StartY=1.5 StartZ=0 EndX=1.9 EndY=1 EndZ=0
    g5: ArcOfCircle CenterX=0 CenterY=2.305 CenterZ=0 NormalX=0 NormalY=0 NormalZ=1 AngleXU=0 Radius=2.305 StartAngle=4.71239 EndAngle=5.68134
  constraints (18):
    c: Distance(g0) = 7
    c: Coincident(g0,g-1)
    c: PointOnObject(g0,g-2)
    c: Distance(g1) = 1
    c: Coincident(g1,g0)
    c: Horizontal(g1)
    c: Distance(g2) = 5.5
    c: Coincident(g2,g1)
    c: Vertical(g2)
    c: Distance(g3) = 0.9
    c: Coincident(g3,g2)
    c: Horizontal(g3)
    c: Distance(g4) = 0.5
    c: Coincident(g4,g3)
    c: Vertical(g4)
    c: Coincident(g5,g4)
    c: Coincident(g5,g0)
    c: PointOnObject(g5,g0)
FEATURE [PartDesign::Revolution] Revolution001
  Angle = 360
  Angle2 = 60
  Axis = (0,2e-16,1)
  Base = (0,0,0)
  FuseOrder = 1
  Placement = pos=(0,0,0) rot=(1,0,0;1.5708rad)
  Profile = -> Sketch028
  ReferenceAxis = -> Sketch028 [V_Axis]
  Reversed = true
  Suppressed = false
  Type = 0
FEATURE [Sketcher::SketchObject] Sketch029
  ArcFitTolerance = 1e-06
  AttachmentSupport = -> [Revolution001]
  ExternalTypes = [0]
  FullyConstrained = true
  MakeInternals = false
  MapMode = 5
  Placement = pos=(0,7e-16,1.5) rot=(0,0,1;3.14159rad)
  _ExternalGeoVersion = 0
  sketch-geometry (6):
    g0: LineSegment StartX=-0.5 StartY=0.866025 StartZ=0 EndX=0.5 EndY=0.866025 EndZ=0
    g1: LineSegment StartX=0.5 StartY=0.866025 StartZ=0 EndX=1 EndY=0 EndZ=0
    g2: LineSegment StartX=0.5 StartY=-0.866025 StartZ=0 EndX=-0.5 EndY=-0.866025 EndZ=0
    g3: LineSegment StartX=-0.5 StartY=-0.866025 StartZ=0 EndX=-1 EndY=0 EndZ=0
    g4: LineSegment StartX=-1 StartY=0 StartZ=0 EndX=-0.5 EndY=0.866025 EndZ=0
    g5: LineSegment StartX=0.5 StartY=-0.866025 StartZ=0 EndX=1 EndY=0 EndZ=0
  constraints (18):
    c: Horizontal(g0)
    c: Coincident(g1,g0)
    c: Horizontal(g2)
    c: Coincident(g3,g2)
    c: Coincident(g4,g3)
    c: Coincident(g4,g0)
    c: DistanceX(g0,g0) = 1
    c: DistanceX(g2,g0) = 0
    c: PointOnObject(g3,g-1)
    c: PointOnObject(g1,g-1)
    c: DistanceX(g2,g2) = 1
    c: Coincident(g5,g2)
    c: Coincident(g5,g1)
    c: Distance(g5,g5) = 1
    c: Distance(g1,g1) = 1
    c: Distance(g4,g4) = 1
    c: DistanceX(g0,g-1) = 0.5
    c: Angle(g4,g0) = 2.0944
FEATURE [PartDesign::Pocket] Pocket017
  BaseFeature = -> Revolution001
  Direction = (0,0,-1)
  Length = 5
  Length2 = 5
  Placement = pos=(0,0,0) rot=(1,0,0;1.5708rad)
  Profile = -> Sketch029
  ReferenceAxis = -> Sketch029 [N_Axis]
  SideType = 0
  Suppressed = false
  Type = 1
  Type2 = 0
FEATURE [PartDesign::Body] Body010  label="HexBolt"
  AllowCompound = false
  Group = -> [Sketch028,Revolution001,Sketch029,Pocket017]
  Origin = -> Origin011
  Tip = -> Pocket017
COMPONENT P12 — same part as P11; its construction recipe is shown at P11.
COMPONENT P13 — same part as P11; its construction recipe is shown at P11.
COMPONENT P14 — same part as P11; its construction recipe is shown at P11.
COMPONENT P15 — same part as P11; its construction recipe is shown at P11.
COMPONENT P16 — same part as P11; its construction recipe is shown at P11.
PROVENANCE & LICENSES
A FreeCAD (.FCStd) document from a public repository crawl; recipes are the document's own serialized feature recipes (and, for linked parts, companion documents' recipes).
License: cern-ohl.
